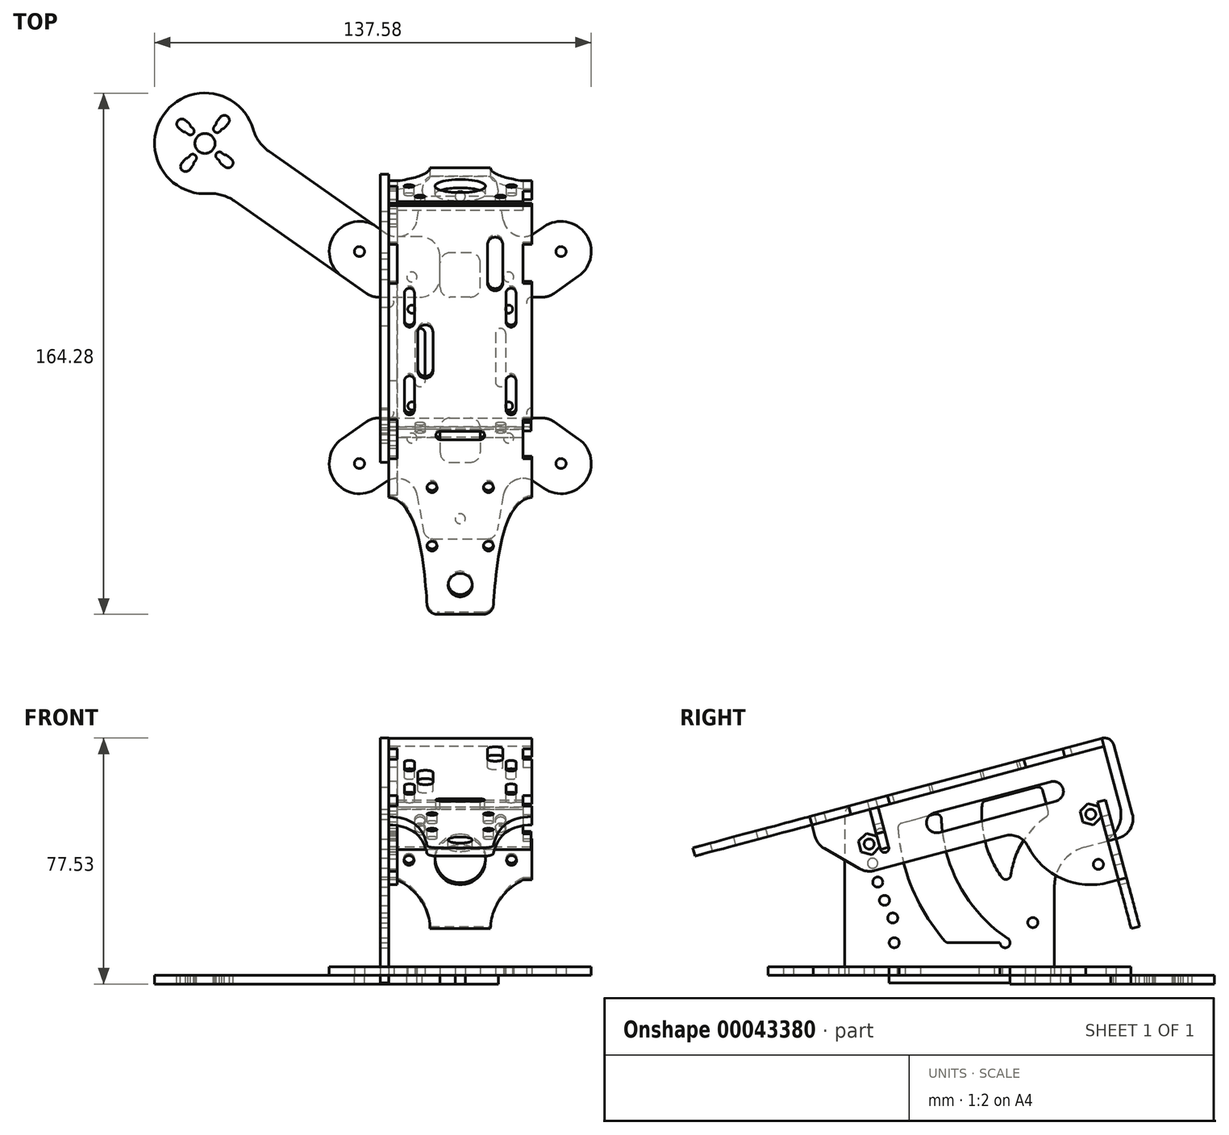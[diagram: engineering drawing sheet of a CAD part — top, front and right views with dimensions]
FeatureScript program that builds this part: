
annotation { "Feature Type Name" : "Feature", "Feature Type Description" : "" }
export const myFeature = defineFeature(function(context is Context, id is Id, definition is map)
    precondition{}
    {
        {
            var Q0;
            Q0=qCreatedBy(makeId("Top.planeOp"),FACE);
            var sketch = newSketch(context, id + "F0", { "sketchPlane" : qUnion([Q0])});
            skCircle(sketch, "E0", {"center": v(0, 0) * mm, "radius": 105 * mm, "construction": true});
            skLineSegment(sketch, "E1", {"start": v(0, 0) * mm, "end": v(-80.43, 67.5) * mm, "construction": true});
            skLineSegment(sketch, "E2", {"start": v(0, 0) * mm, "end": v(80.43, 67.5) * mm, "construction": true});
            skLineSegment(sketch, "E3", {"start": v(-80.43, 67.5) * mm, "end": v(80.43, 67.5) * mm, "construction": true});
            skLineSegment(sketch, "E4", {"start": v(0, 0) * mm, "end": v(80.43, -67.5) * mm, "construction": true});
            skLineSegment(sketch, "E5", {"start": v(80.43, -67.5) * mm, "end": v(-80.43, -67.5) * mm, "construction": true});
            skLineSegment(sketch, "E6", {"start": v(-80.43, -67.5) * mm, "end": v(0, 0) * mm, "construction": true});
            skSolve(sketch);
        }
        {
            var Q0;
            Q0=qCreatedBy(makeId("Top.planeOp"),FACE);
            var sketch = newSketch(context, id + "F1", { "sketchPlane" : qUnion([Q0])});
            skCircle(sketch, "E7", {"center": v(-80.43, 67.5) * mm, "radius": 15.88 * mm});
            skArc(sketch, "E8", {"start": v(-74.18, 60.17) * mm, "mid": v(-71.94, 60.37) * mm, "end": v(-72.14, 62.6) * mm});
            skArc(sketch, "E9", {"start": v(-75.88, 62.11) * mm, "mid": v(-75.7, 61.57) * mm, "end": v(-75.33, 61.13) * mm});
            skLineSegment(sketch, "E10", {"start": v(-80.43, 67.5) * mm, "end": v(-68.27, 57.29) * mm, "construction": true});
            skArc(sketch, "E11", {"start": v(-75.07, 64.55) * mm, "mid": v(-76.75, 64.4) * mm, "end": v(-76.6, 62.72) * mm});
            skLineSegment(sketch, "E12", {"start": v(-75.07, 64.55) * mm, "end": v(-74.35, 63.94) * mm});
            skLineSegment(sketch, "E13", {"start": v(-76.6, 62.72) * mm, "end": v(-75.88, 62.11) * mm});
            skLineSegment(sketch, "E14", {"start": v(-73.29, 63.57) * mm, "end": v(-72.14, 62.6) * mm});
            skLineSegment(sketch, "E15", {"start": v(-75.33, 61.13) * mm, "end": v(-74.18, 60.17) * mm});
            skArc(sketch, "E16.trimOffspring", {"start": v(-73.29, 63.57) * mm, "mid": v(-73.78, 63.85) * mm, "end": v(-74.35, 63.94) * mm});
            skArc(sketch, "E17.1.0", {"start": v(-77.5, 72.85) * mm, "mid": v(-77.34, 71.18) * mm, "end": v(-75.67, 71.32) * mm});
            skArc(sketch, "E17.1.1", {"start": v(-73.11, 73.75) * mm, "mid": v(-73.3, 75.99) * mm, "end": v(-75.54, 75.8) * mm});
            skArc(sketch, "E17.1.2", {"start": v(-76.5, 74.64) * mm, "mid": v(-76.8, 74.15) * mm, "end": v(-76.88, 73.58) * mm});
            skLineSegment(sketch, "E17.1.3", {"start": v(-74.08, 72.6) * mm, "end": v(-73.11, 73.75) * mm});
            skLineSegment(sketch, "E17.1.4", {"start": v(-76.5, 74.64) * mm, "end": v(-75.54, 75.8) * mm});
            skLineSegment(sketch, "E17.1.5", {"start": v(-75.67, 71.32) * mm, "end": v(-75.06, 72.05) * mm});
            skLineSegment(sketch, "E17.1.6", {"start": v(-77.5, 72.85) * mm, "end": v(-76.88, 73.58) * mm});
            skArc(sketch, "E17.1.7", {"start": v(-75.06, 72.05) * mm, "mid": v(-74.52, 72.24) * mm, "end": v(-74.08, 72.6) * mm});
            skArc(sketch, "E17.2.0", {"start": v(-85.8, 70.44) * mm, "mid": v(-84.12, 70.58) * mm, "end": v(-84.27, 72.26) * mm});
            skArc(sketch, "E17.2.1", {"start": v(-86.7, 74.82) * mm, "mid": v(-88.93, 74.62) * mm, "end": v(-88.73, 72.38) * mm});
            skArc(sketch, "E17.2.2", {"start": v(-87.58, 71.42) * mm, "mid": v(-87.09, 71.14) * mm, "end": v(-86.52, 71.05) * mm});
            skLineSegment(sketch, "E17.2.3", {"start": v(-85.54, 73.85) * mm, "end": v(-86.7, 74.82) * mm});
            skLineSegment(sketch, "E17.2.4", {"start": v(-87.58, 71.42) * mm, "end": v(-88.73, 72.38) * mm});
            skLineSegment(sketch, "E17.2.5", {"start": v(-84.27, 72.26) * mm, "end": v(-85, 72.87) * mm});
            skLineSegment(sketch, "E17.2.6", {"start": v(-85.8, 70.44) * mm, "end": v(-86.52, 71.05) * mm});
            skArc(sketch, "E17.2.7", {"start": v(-85, 72.87) * mm, "mid": v(-85.18, 73.41) * mm, "end": v(-85.54, 73.85) * mm});
            skArc(sketch, "E17.3.0", {"start": v(-83.38, 62.13) * mm, "mid": v(-83.53, 63.8) * mm, "end": v(-85.2, 63.66) * mm});
            skArc(sketch, "E17.3.1", {"start": v(-87.76, 61.24) * mm, "mid": v(-87.56, 59) * mm, "end": v(-85.33, 59.2) * mm});
            skArc(sketch, "E17.3.2", {"start": v(-84.36, 60.34) * mm, "mid": v(-84.08, 60.84) * mm, "end": v(-83.99, 61.4) * mm});
            skLineSegment(sketch, "E17.3.3", {"start": v(-86.8, 62.38) * mm, "end": v(-87.76, 61.24) * mm});
            skLineSegment(sketch, "E17.3.4", {"start": v(-84.36, 60.34) * mm, "end": v(-85.33, 59.2) * mm});
            skLineSegment(sketch, "E17.3.5", {"start": v(-85.2, 63.66) * mm, "end": v(-85.81, 62.93) * mm});
            skLineSegment(sketch, "E17.3.6", {"start": v(-83.38, 62.13) * mm, "end": v(-83.99, 61.4) * mm});
            skArc(sketch, "E17.3.7", {"start": v(-85.81, 62.93) * mm, "mid": v(-86.35, 62.75) * mm, "end": v(-86.8, 62.38) * mm});
            skCircle(sketch, "E18", {"center": v(-80.43, 67.5) * mm, "radius": 3.18 * mm});
            skCircle(sketch, "E19", {"center": v(-80.43, -67.5) * mm, "radius": 15.88 * mm});
            skLineSegment(sketch, "E20", {"start": v(-80.43, -67.5) * mm, "end": v(-70.23, -79.65) * mm, "construction": true});
            skCircle(sketch, "E21", {"center": v(-80.43, -67.5) * mm, "radius": 3.18 * mm});
            skArc(sketch, "E22.3.1", {"start": v(-88.73, -72.38) * mm, "mid": v(-88.93, -74.62) * mm, "end": v(-86.7, -74.82) * mm});
            skArc(sketch, "E23", {"start": v(-75.54, -75.8) * mm, "mid": v(-73.3, -75.99) * mm, "end": v(-73.11, -73.75) * mm});
            skArc(sketch, "E22.3.0", {"start": v(-84.27, -72.26) * mm, "mid": v(-84.12, -70.58) * mm, "end": v(-85.8, -70.44) * mm});
            skLineSegment(sketch, "E22.3.4", {"start": v(-85.54, -73.85) * mm, "end": v(-86.7, -74.82) * mm});
            skLineSegment(sketch, "E22.2.3", {"start": v(-84.36, -60.34) * mm, "end": v(-85.33, -59.2) * mm});
            skArc(sketch, "E22.2.1", {"start": v(-85.33, -59.2) * mm, "mid": v(-87.56, -59) * mm, "end": v(-87.76, -61.24) * mm});
            skArc(sketch, "E22.3.7", {"start": v(-86.52, -71.05) * mm, "mid": v(-87.09, -71.14) * mm, "end": v(-87.58, -71.42) * mm});
            skLineSegment(sketch, "E22.1.4", {"start": v(-75.33, -61.13) * mm, "end": v(-74.18, -60.17) * mm});
            skLineSegment(sketch, "E22.3.5", {"start": v(-85.8, -70.44) * mm, "end": v(-86.52, -71.05) * mm});
            skLineSegment(sketch, "E22.3.3", {"start": v(-87.58, -71.42) * mm, "end": v(-88.73, -72.38) * mm});
            skArc(sketch, "E24", {"start": v(-75.67, -71.32) * mm, "mid": v(-77.34, -71.18) * mm, "end": v(-77.5, -72.85) * mm});
            skLineSegment(sketch, "E22.3.6", {"start": v(-84.27, -72.26) * mm, "end": v(-85, -72.87) * mm});
            skArc(sketch, "E22.1.1", {"start": v(-72.14, -62.6) * mm, "mid": v(-71.94, -60.37) * mm, "end": v(-74.18, -60.17) * mm});
            skArc(sketch, "E22.3.2", {"start": v(-85.54, -73.85) * mm, "mid": v(-85.18, -73.41) * mm, "end": v(-85, -72.87) * mm});
            skLineSegment(sketch, "E22.2.6", {"start": v(-85.2, -63.66) * mm, "end": v(-85.81, -62.93) * mm});
            skArc(sketch, "E22.1.7", {"start": v(-74.35, -63.94) * mm, "mid": v(-73.78, -63.85) * mm, "end": v(-73.29, -63.57) * mm});
            skArc(sketch, "E22.2.7", {"start": v(-83.99, -61.4) * mm, "mid": v(-84.08, -60.84) * mm, "end": v(-84.36, -60.34) * mm});
            skLineSegment(sketch, "E22.1.3", {"start": v(-73.29, -63.57) * mm, "end": v(-72.14, -62.6) * mm});
            skLineSegment(sketch, "E22.2.5", {"start": v(-83.38, -62.13) * mm, "end": v(-83.99, -61.4) * mm});
            skLineSegment(sketch, "E22.1.5", {"start": v(-75.07, -64.55) * mm, "end": v(-74.35, -63.94) * mm});
            skLineSegment(sketch, "E22.2.4", {"start": v(-86.8, -62.38) * mm, "end": v(-87.76, -61.24) * mm});
            skArc(sketch, "E25", {"start": v(-76.88, -73.58) * mm, "mid": v(-76.8, -74.15) * mm, "end": v(-76.5, -74.64) * mm});
            skArc(sketch, "E22.2.2", {"start": v(-86.8, -62.38) * mm, "mid": v(-86.35, -62.75) * mm, "end": v(-85.81, -62.93) * mm});
            skArc(sketch, "E22.2.0", {"start": v(-85.2, -63.66) * mm, "mid": v(-83.53, -63.8) * mm, "end": v(-83.38, -62.13) * mm});
            skLineSegment(sketch, "E26", {"start": v(-77.5, -72.85) * mm, "end": v(-76.88, -73.58) * mm});
            skLineSegment(sketch, "E27", {"start": v(-74.08, -72.6) * mm, "end": v(-73.11, -73.75) * mm});
            skLineSegment(sketch, "E28", {"start": v(-76.5, -74.64) * mm, "end": v(-75.54, -75.8) * mm});
            skArc(sketch, "E29.trimOffspring", {"start": v(-74.08, -72.6) * mm, "mid": v(-74.52, -72.24) * mm, "end": v(-75.06, -72.05) * mm});
            skArc(sketch, "E22.1.0", {"start": v(-76.6, -62.72) * mm, "mid": v(-76.75, -64.4) * mm, "end": v(-75.07, -64.55) * mm});
            skArc(sketch, "E22.1.2", {"start": v(-75.33, -61.13) * mm, "mid": v(-75.7, -61.57) * mm, "end": v(-75.88, -62.11) * mm});
            skLineSegment(sketch, "E30", {"start": v(-75.67, -71.32) * mm, "end": v(-75.06, -72.05) * mm});
            skLineSegment(sketch, "E22.1.6", {"start": v(-76.6, -62.72) * mm, "end": v(-75.88, -62.11) * mm});
            skSolve(sketch);
        }
        {
            var Q0;
            Q0=qCreatedBy(makeId("Top.planeOp"),FACE);
            var sketch = newSketch(context, id + "F2", { "sketchPlane" : qUnion([Q0])});
            skCircle(sketch, "E31", {"center": v(-80.43, 67.5) * mm, "radius": 63.5 * mm, "construction": true});
            skLineSegment(sketch, "E32.bottom", {"start": v(-18, 18) * mm, "end": v(18, 18) * mm, "construction": true});
            skLineSegment(sketch, "E32.top", {"start": v(-18, -18) * mm, "end": v(18, -18) * mm, "construction": true});
            skLineSegment(sketch, "E32.left", {"start": v(-18, 18) * mm, "end": v(-18, -18) * mm, "construction": true});
            skLineSegment(sketch, "E32.right", {"start": v(18, 18) * mm, "end": v(18, -18) * mm, "construction": true});
            skPoint(sketch, "E33", {"position": v(0, 18) * mm});
            skPoint(sketch, "E34", {"position": v(18, 0) * mm});
            skCircle(sketch, "E35", {"center": v(-80.43, -67.5) * mm, "radius": 63.5 * mm, "construction": true});
            skCircle(sketch, "E36", {"center": v(80.43, -67.5) * mm, "radius": 63.5 * mm, "construction": true});
            skCircle(sketch, "E37", {"center": v(80.43, 67.5) * mm, "radius": 63.5 * mm, "construction": true});
            skSolve(sketch);
        }
        {
            var Q0;
            Q0=qCreatedBy(makeId("Top.planeOp"),FACE);
            var sketch = newSketch(context, id + "F3", { "sketchPlane" : qUnion([Q0])});
            skArc(sketch, "E38", {"start": v(-65.18, 71.88) * mm, "mid": v(-93.44, 76.6) * mm, "end": v(-79.34, 51.66) * mm});
            skLineSegment(sketch, "E39", {"start": v(-80.43, 67.5) * mm, "end": v(5.58, 7.27) * mm, "construction": true});
            skLineSegment(sketch, "E40.0", {"start": v(-71.19, 49.39) * mm, "end": v(-29.5, 20.2) * mm});
            skLineSegment(sketch, "E41.0", {"start": v(-60.26, 65) * mm, "end": v(-23.5, 39.25) * mm});
            skPoint(sketch, "E42.visualSharp", {"position": v(-64.57, 68.01) * mm});
            skArc(sketch, "E42.filletArc", {"start": v(-65.18, 71.88) * mm, "mid": v(-63.31, 68.02) * mm, "end": v(-60.26, 65) * mm});
            skPoint(sketch, "E43.visualSharp", {"position": v(-75.5, 52.4) * mm});
            skArc(sketch, "E43.filletArc", {"start": v(-71.19, 49.39) * mm, "mid": v(-75.07, 51.22) * mm, "end": v(-79.34, 51.66) * mm});
            skLineSegment(sketch, "E44", {"start": v(-12.7, 38.1) * mm, "end": v(-19.85, 38.1) * mm});
            skArc(sketch, "E45.filletArc", {"start": v(-23.5, 39.25) * mm, "mid": v(-21.76, 38.4) * mm, "end": v(-19.85, 38.1) * mm});
            skLineSegment(sketch, "E46", {"start": v(0, 0) * mm, "end": v(0, 111.42) * mm, "construction": true});
            skLineSegment(sketch, "E47", {"start": v(-22.5, -33.02) * mm, "end": v(-22.5, 33.02) * mm, "construction": true});
            skLineSegment(sketch, "E48", {"start": v(-25.86, 19.05) * mm, "end": v(-12.7, 19.05) * mm});
            skLineSegment(sketch, "E49", {"start": v(-6.35, 25.4) * mm, "end": v(-6.35, 31.75) * mm});
            skPoint(sketch, "E50.orphan", {"position": v(0, 19.05) * mm});
            skPoint(sketch, "E51.visualSharp", {"position": v(-6.35, 38.1) * mm});
            skArc(sketch, "E51.filletArc", {"start": v(-6.35, 31.75) * mm, "mid": v(-8.2, 36.24) * mm, "end": v(-12.7, 38.1) * mm});
            skPoint(sketch, "E52.visualSharp", {"position": v(-6.35, 19.05) * mm});
            skArc(sketch, "E52.filletArc", {"start": v(-12.7, 19.05) * mm, "mid": v(-8.2, 20.9) * mm, "end": v(-6.35, 25.4) * mm});
            skArc(sketch, "E53.filletArc", {"start": v(-29.5, 20.2) * mm, "mid": v(-27.76, 19.34) * mm, "end": v(-25.86, 19.05) * mm});
            skSolve(sketch);
        }
        {
            var Q0;
            Q0=qCreatedBy(makeId("Right.planeOp"),FACE);
            var sketch = newSketch(context, id + "F4", { "sketchPlane" : qUnion([Q0])});
            skLineSegment(sketch, "E54", {"start": v(-18.08, 54.87) * mm, "end": v(54.37, 74.29) * mm, "construction": true});
            skLineSegment(sketch, "E55", {"start": v(54.37, 74.29) * mm, "end": v(58.77, 57.87) * mm, "construction": true});
            skLineSegment(sketch, "E56", {"start": v(58.77, 57.87) * mm, "end": v(-13.68, 38.45) * mm, "construction": true});
            skLineSegment(sketch, "E57", {"start": v(-13.68, 38.45) * mm, "end": v(-18.08, 54.87) * mm, "construction": true});
            skLineSegment(sketch, "E58", {"start": v(33.02, 0) * mm, "end": v(33.02, 29.72) * mm});
            skCircle(sketch, "E59", {"center": v(50.8, 50.8) * mm, "radius": 1.59 * mm});
            skLineSegment(sketch, "E60", {"start": v(58.58, 46.3) * mm, "end": v(42.43, 41.98) * mm});
            skArc(sketch, "E61.filletArc", {"start": v(42.43, 41.98) * mm, "mid": v(35.64, 37.45) * mm, "end": v(33.02, 29.72) * mm});
            skLineSegment(sketch, "E62", {"start": v(63.07, 54.09) * mm, "end": v(58.14, 72.49) * mm});
            skArc(sketch, "E63.filletArc", {"start": v(58.58, 46.3) * mm, "mid": v(62.43, 49.27) * mm, "end": v(63.07, 54.09) * mm});
            skLineSegment(sketch, "E64", {"start": v(50.36, 76.98) * mm, "end": v(-28.31, 55.9) * mm});
            skLineSegment(sketch, "E65", {"start": v(0, 0) * mm, "end": v(135.9, 0) * mm, "construction": true});
            skPoint(sketch, "E66.visualSharp", {"position": v(56.5, 78.62) * mm});
            skArc(sketch, "E66.filletArc", {"start": v(58.14, 72.49) * mm, "mid": v(55.18, 76.34) * mm, "end": v(50.36, 76.98) * mm});
            skLineSegment(sketch, "E67", {"start": v(-33.02, 0) * mm, "end": v(-33.02, 49.76) * mm});
            skPoint(sketch, "E68.visualSharp", {"position": v(-33.02, 54.64) * mm});
            skArc(sketch, "E68.filletArc", {"start": v(-28.31, 55.9) * mm, "mid": v(-31.7, 53.63) * mm, "end": v(-33.02, 49.76) * mm});
            skCircle(sketch, "E69", {"center": v(50.8, 50.8) * mm, "radius": 77.48 * mm, "construction": true});
            skLineSegment(sketch, "E70", {"start": v(50.8, 50.8) * mm, "end": v(-26.67, 49.76) * mm, "construction": true});
            skLineSegment(sketch, "E71", {"start": v(50.8, 50.8) * mm, "end": v(-21.64, 23.33) * mm, "construction": true});
            skCircle(sketch, "E72.cCircle", {"center": v(50.8, 50.8) * mm, "radius": 3 * mm, "construction": true});
            skLineSegment(sketch, "E72.0", {"start": v(49.9, 54.15) * mm, "end": v(53.25, 53.25) * mm, "construction": true});
            skLineSegment(sketch, "E72.1", {"start": v(53.25, 53.25) * mm, "end": v(54.15, 49.9) * mm, "construction": true});
            skLineSegment(sketch, "E72.2", {"start": v(54.15, 49.9) * mm, "end": v(51.7, 47.45) * mm, "construction": true});
            skLineSegment(sketch, "E72.3", {"start": v(51.7, 47.45) * mm, "end": v(48.35, 48.35) * mm, "construction": true});
            skLineSegment(sketch, "E72.4", {"start": v(48.35, 48.35) * mm, "end": v(47.45, 51.7) * mm, "construction": true});
            skLineSegment(sketch, "E72.5", {"start": v(47.45, 51.7) * mm, "end": v(49.9, 54.15) * mm, "construction": true});
            skPoint(sketch, "E72.0.midPoint", {"position": v(51.58, 53.7) * mm});
            skCircle(sketch, "E73", {"center": v(-26.67, 49.76) * mm, "radius": 1.59 * mm});
            skLineSegment(sketch, "E74", {"start": v(50.8, 50.8) * mm, "end": v(-25.31, 36.33) * mm, "construction": true});
            skLineSegment(sketch, "E75", {"start": v(50.8, 50.8) * mm, "end": v(-23.76, 29.75) * mm, "construction": true});
            skCircle(sketch, "E76", {"center": v(-25.31, 36.33) * mm, "radius": 1.59 * mm});
            skCircle(sketch, "E77", {"center": v(-21.64, 23.33) * mm, "radius": 1.59 * mm});
            skLineSegment(sketch, "E78", {"start": v(50.8, 50.8) * mm, "end": v(-26.28, 43.02) * mm, "construction": true});
            skCircle(sketch, "E79", {"center": v(-26.28, 43.02) * mm, "radius": 1.59 * mm});
            skCircle(sketch, "E80", {"center": v(-23.76, 29.75) * mm, "radius": 1.59 * mm});
            skCircle(sketch, "E81.cCircle", {"center": v(-26.67, 49.76) * mm, "radius": 3 * mm, "construction": true});
            skLineSegment(sketch, "E81.0", {"start": v(-25.77, 53.11) * mm, "end": v(-23.32, 50.66) * mm, "construction": true});
            skLineSegment(sketch, "E81.1", {"start": v(-23.32, 50.66) * mm, "end": v(-24.22, 47.31) * mm, "construction": true});
            skLineSegment(sketch, "E81.2", {"start": v(-24.22, 47.31) * mm, "end": v(-27.57, 46.42) * mm, "construction": true});
            skLineSegment(sketch, "E81.3", {"start": v(-27.57, 46.42) * mm, "end": v(-30.02, 48.87) * mm, "construction": true});
            skLineSegment(sketch, "E81.4", {"start": v(-30.02, 48.87) * mm, "end": v(-29.12, 52.21) * mm, "construction": true});
            skLineSegment(sketch, "E81.5", {"start": v(-29.12, 52.21) * mm, "end": v(-25.77, 53.11) * mm, "construction": true});
            skPoint(sketch, "E81.0.midPoint", {"position": v(-24.55, 51.89) * mm});
            skLineSegment(sketch, "E82.0", {"start": v(51.06, 74.38) * mm, "end": v(-39.05, 50.23) * mm, "construction": true});
            skLineSegment(sketch, "E83", {"start": v(42.03, 71.96) * mm, "end": v(56.53, 17.82) * mm, "construction": true});
            skSolve(sketch);
        }
        {
            var Q0;
            Q0 = qSketchRegion(id + "F3", true);
            extrude(context, id + "F5", {"entities" : qUnion([Q0]), "oppositeDirection" : true, "depth" : 2.7 * mm});
        }
        {
            var Q0;
            Q0=makeQuery(id+"F5.opExtrude","CAP_FACE",FACE,{"disambiguationData":[OSD([sQuery(id+"F3.wireOp",EDGE,"E38"),sQuery(id+"F3.wireOp",EDGE,"E40.0"),sQuery(id+"F3.wireOp",EDGE,"E41.0"),sQuery(id+"F3.wireOp",EDGE,"E42.filletArc"),sQuery(id+"F3.wireOp",EDGE,"E43.filletArc"),sQuery(id+"F3.wireOp",EDGE,"E44"),sQuery(id+"F3.wireOp",EDGE,"E45.filletArc"),sQuery(id+"F3.wireOp",EDGE,"3483ba9e-9ece-47d6-9597-e3f51a3c630d"),sQuery(id+"F3.wireOp",EDGE,"183f9baa-443e-4921-8196-529d93f579a4"),sQuery(id+"F3.wireOp",EDGE,"E48"),sQuery(id+"F3.wireOp",EDGE,"dc9fa72e-4bdb-43c7-b6c3-07b077150070"),sQuery(id+"F3.wireOp",EDGE,"fd774d7d-7de3-4750-95d2-ba5d1b0ac5d5.filletArc"),sQuery(id+"F3.wireOp",EDGE,"888af924-2e86-4a76-b76f-690ec0a1ca8d.filletArc"),sQuery(id+"F3.wireOp",EDGE,"E49")])],"isStart":true});
            var sketch = newSketch(context, id + "F6", { "sketchPlane" : qUnion([Q0])});
            skLineSegment(sketch, "E84", {"start": v(-80.43, 67.5) * mm, "end": v(-31.75, 33.4) * mm, "construction": true});
            skCircle(sketch, "E85", {"center": v(-31.75, 33.4) * mm, "radius": 1.59 * mm});
            skArc(sketch, "E86.0", {"start": v(-77.5, 72.85) * mm, "mid": v(-77.34, 71.18) * mm, "end": v(-75.67, 71.32) * mm});
            skLineSegment(sketch, "E86.1", {"start": v(-77.5, 72.85) * mm, "end": v(-76.88, 73.58) * mm});
            skArc(sketch, "E86.2", {"start": v(-76.5, 74.64) * mm, "mid": v(-76.8, 74.15) * mm, "end": v(-76.88, 73.58) * mm});
            skLineSegment(sketch, "E86.3", {"start": v(-76.5, 74.64) * mm, "end": v(-75.54, 75.8) * mm});
            skArc(sketch, "E86.4", {"start": v(-73.11, 73.75) * mm, "mid": v(-73.3, 75.99) * mm, "end": v(-75.54, 75.8) * mm});
            skLineSegment(sketch, "E86.5", {"start": v(-74.08, 72.6) * mm, "end": v(-73.11, 73.75) * mm});
            skArc(sketch, "E86.6", {"start": v(-75.06, 72.05) * mm, "mid": v(-74.52, 72.24) * mm, "end": v(-74.08, 72.6) * mm});
            skLineSegment(sketch, "E86.7", {"start": v(-75.67, 71.32) * mm, "end": v(-75.06, 72.05) * mm});
            skArc(sketch, "E86.8", {"start": v(-75.07, 64.55) * mm, "mid": v(-76.75, 64.4) * mm, "end": v(-76.6, 62.72) * mm});
            skLineSegment(sketch, "E86.9", {"start": v(-75.07, 64.55) * mm, "end": v(-74.35, 63.94) * mm});
            skArc(sketch, "E86.10", {"start": v(-73.29, 63.57) * mm, "mid": v(-73.78, 63.85) * mm, "end": v(-74.35, 63.94) * mm});
            skLineSegment(sketch, "E86.11", {"start": v(-73.29, 63.57) * mm, "end": v(-72.14, 62.6) * mm});
            skArc(sketch, "E86.12", {"start": v(-74.18, 60.17) * mm, "mid": v(-71.94, 60.37) * mm, "end": v(-72.14, 62.6) * mm});
            skLineSegment(sketch, "E86.13", {"start": v(-75.33, 61.13) * mm, "end": v(-74.18, 60.17) * mm});
            skArc(sketch, "E86.14", {"start": v(-75.88, 62.11) * mm, "mid": v(-75.7, 61.57) * mm, "end": v(-75.33, 61.13) * mm});
            skLineSegment(sketch, "E86.15", {"start": v(-76.6, 62.72) * mm, "end": v(-75.88, 62.11) * mm});
            skCircle(sketch, "E86.16", {"center": v(-80.43, 67.5) * mm, "radius": 3.18 * mm});
            skArc(sketch, "E86.17", {"start": v(-85.8, 70.44) * mm, "mid": v(-84.12, 70.58) * mm, "end": v(-84.27, 72.26) * mm});
            skLineSegment(sketch, "E86.18", {"start": v(-85.8, 70.44) * mm, "end": v(-86.52, 71.05) * mm});
            skArc(sketch, "E86.19", {"start": v(-87.58, 71.42) * mm, "mid": v(-87.09, 71.14) * mm, "end": v(-86.52, 71.05) * mm});
            skLineSegment(sketch, "E86.20", {"start": v(-87.58, 71.42) * mm, "end": v(-88.73, 72.38) * mm});
            skArc(sketch, "E86.21", {"start": v(-86.7, 74.82) * mm, "mid": v(-88.93, 74.62) * mm, "end": v(-88.73, 72.38) * mm});
            skLineSegment(sketch, "E86.22", {"start": v(-85.54, 73.85) * mm, "end": v(-86.7, 74.82) * mm});
            skArc(sketch, "E86.23", {"start": v(-85, 72.87) * mm, "mid": v(-85.18, 73.41) * mm, "end": v(-85.54, 73.85) * mm});
            skLineSegment(sketch, "E86.24", {"start": v(-84.27, 72.26) * mm, "end": v(-85, 72.87) * mm});
            skArc(sketch, "E86.25", {"start": v(-83.38, 62.13) * mm, "mid": v(-83.53, 63.8) * mm, "end": v(-85.2, 63.66) * mm});
            skLineSegment(sketch, "E86.26", {"start": v(-85.2, 63.66) * mm, "end": v(-85.81, 62.93) * mm});
            skLineSegment(sketch, "E86.27", {"start": v(-83.38, 62.13) * mm, "end": v(-83.99, 61.4) * mm});
            skArc(sketch, "E86.28", {"start": v(-84.36, 60.34) * mm, "mid": v(-84.08, 60.84) * mm, "end": v(-83.99, 61.4) * mm});
            skLineSegment(sketch, "E86.29", {"start": v(-84.36, 60.34) * mm, "end": v(-85.33, 59.2) * mm});
            skArc(sketch, "E86.30", {"start": v(-87.76, 61.24) * mm, "mid": v(-87.56, 59) * mm, "end": v(-85.33, 59.2) * mm});
            skLineSegment(sketch, "E86.31", {"start": v(-86.8, 62.38) * mm, "end": v(-87.76, 61.24) * mm});
            skArc(sketch, "E86.32", {"start": v(-85.81, 62.93) * mm, "mid": v(-86.35, 62.75) * mm, "end": v(-86.8, 62.38) * mm});
            skCircle(sketch, "E87", {"center": v(-15.24, 25.4) * mm, "radius": 1.59 * mm});
            skSolve(sketch);
        }
        {
            var Q0;
            Q0 = qSketchRegion(id + "F6", true);
            var Q1;
            Q1=makeQuery(id+"F5.opExtrude","CAP_FACE",FACE,{"disambiguationData":[OSD([sQuery(id+"F3.wireOp",EDGE,"E38"),sQuery(id+"F3.wireOp",EDGE,"E40.0"),sQuery(id+"F3.wireOp",EDGE,"E41.0"),sQuery(id+"F3.wireOp",EDGE,"E42.filletArc"),sQuery(id+"F3.wireOp",EDGE,"E43.filletArc"),sQuery(id+"F3.wireOp",EDGE,"E44"),sQuery(id+"F3.wireOp",EDGE,"E45.filletArc"),sQuery(id+"F3.wireOp",EDGE,"3483ba9e-9ece-47d6-9597-e3f51a3c630d"),sQuery(id+"F3.wireOp",EDGE,"183f9baa-443e-4921-8196-529d93f579a4"),sQuery(id+"F3.wireOp",EDGE,"E48"),sQuery(id+"F3.wireOp",EDGE,"dc9fa72e-4bdb-43c7-b6c3-07b077150070"),sQuery(id+"F3.wireOp",EDGE,"fd774d7d-7de3-4750-95d2-ba5d1b0ac5d5.filletArc"),sQuery(id+"F3.wireOp",EDGE,"888af924-2e86-4a76-b76f-690ec0a1ca8d.filletArc"),sQuery(id+"F3.wireOp",EDGE,"E49")])],"isStart":false});
            extrude(context, id + "F7", {"entities" : qUnion([Q0]), "operationType" : NewBodyOperationType.REMOVE, "endBound" : BoundingType.UP_TO_SURFACE, "oppositeDirection" : true, "endBoundEntityFace" : qUnion([Q1]), "depth" : 25.4 * mm});
        }
        {
            var Q0;
            Q0=qCreatedBy(makeId("Top.planeOp"),FACE);
            var sketch = newSketch(context, id + "F8", { "sketchPlane" : qUnion([Q0])});
            skLineSegment(sketch, "E88.0", {"start": v(-37.21, 25.6) * mm, "end": v(-29.5, 20.2) * mm});
            skArc(sketch, "E88.1", {"start": v(-29.5, 20.2) * mm, "mid": v(-27.76, 19.34) * mm, "end": v(-25.86, 19.05) * mm});
            skLineSegment(sketch, "E88.2", {"start": v(-25.86, 19.05) * mm, "end": v(-22.5, 19.05) * mm});
            skLineSegment(sketch, "E88.3", {"start": v(-26.29, 41.2) * mm, "end": v(-23.5, 39.25) * mm});
            skArc(sketch, "E89", {"start": v(-26.29, 41.2) * mm, "mid": v(-39.55, 38.87) * mm, "end": v(-37.21, 25.6) * mm});
            skArc(sketch, "E90", {"start": v(-23.5, 39.25) * mm, "mid": v(-17.42, 38.58) * mm, "end": v(-13.6, 43.35) * mm});
            skLineSegment(sketch, "E91", {"start": v(-22.5, 0) * mm, "end": v(-22.5, 15.88) * mm});
            skArc(sketch, "E92", {"start": v(-22.5, 15.88) * mm, "mid": v(-20.92, 17.46) * mm, "end": v(-22.5, 19.05) * mm});
            skPoint(sketch, "E93.orphan", {"position": v(-12.7, 19.05) * mm});
            skLineSegment(sketch, "E94", {"start": v(-8.5, 57.15) * mm, "end": v(0, 57.15) * mm});
            skLineSegment(sketch, "E95", {"start": v(-13.6, 43.35) * mm, "end": v(-11.62, 54.53) * mm});
            skPoint(sketch, "E96.visualSharp", {"position": v(-11.16, 57.15) * mm});
            skArc(sketch, "E96.filletArc", {"start": v(-8.5, 57.15) * mm, "mid": v(-10.54, 56.4) * mm, "end": v(-11.62, 54.53) * mm});
            skLineSegment(sketch, "E97.MirrorCS", {"start": v(26.29, 41.2) * mm, "end": v(23.5, 39.25) * mm});
            skLineSegment(sketch, "E98.MirrorCS", {"start": v(25.86, 19.05) * mm, "end": v(22.5, 19.05) * mm});
            skArc(sketch, "E99.MirrorCS", {"start": v(29.5, 20.2) * mm, "mid": v(27.76, 19.34) * mm, "end": v(25.86, 19.05) * mm});
            skArc(sketch, "E100.MirrorCS", {"start": v(22.5, 15.88) * mm, "mid": v(20.92, 17.46) * mm, "end": v(22.5, 19.05) * mm});
            skArc(sketch, "E101.MirrorCS", {"start": v(8.5, 57.15) * mm, "mid": v(10.54, 56.4) * mm, "end": v(11.62, 54.53) * mm});
            skLineSegment(sketch, "E102.MirrorCS", {"start": v(8.5, 57.15) * mm, "end": v(0, 57.15) * mm});
            skPoint(sketch, "E103.MirrorP", {"position": v(11.16, 57.15) * mm});
            skLineSegment(sketch, "E104.MirrorCS", {"start": v(13.6, 43.35) * mm, "end": v(11.62, 54.53) * mm});
            skArc(sketch, "E105.MirrorCS", {"start": v(23.5, 39.25) * mm, "mid": v(17.42, 38.58) * mm, "end": v(13.6, 43.35) * mm});
            skArc(sketch, "E106.MirrorCS", {"start": v(26.29, 41.2) * mm, "mid": v(39.55, 38.87) * mm, "end": v(37.21, 25.6) * mm});
            skLineSegment(sketch, "E107.MirrorCS", {"start": v(37.21, 25.6) * mm, "end": v(29.5, 20.2) * mm});
            skPoint(sketch, "E108.MirrorP", {"position": v(12.7, 19.05) * mm});
            skLineSegment(sketch, "E109.MirrorCS", {"start": v(22.5, 0) * mm, "end": v(22.5, 15.88) * mm});
            skArc(sketch, "E110.MirrorCS", {"start": v(-8.5, -57.15) * mm, "mid": v(-10.54, -56.4) * mm, "end": v(-11.62, -54.53) * mm});
            skArc(sketch, "E111.MirrorCS", {"start": v(8.5, -57.15) * mm, "mid": v(10.54, -56.4) * mm, "end": v(11.62, -54.53) * mm});
            skLineSegment(sketch, "E112.MirrorCS", {"start": v(-26.29, -41.2) * mm, "end": v(-23.5, -39.25) * mm});
            skLineSegment(sketch, "E113.MirrorCS", {"start": v(26.29, -41.2) * mm, "end": v(23.5, -39.25) * mm});
            skLineSegment(sketch, "E114.MirrorCS", {"start": v(-37.21, -25.6) * mm, "end": v(-29.5, -20.2) * mm});
            skArc(sketch, "E115.MirrorCS", {"start": v(-29.5, -20.2) * mm, "mid": v(-27.76, -19.34) * mm, "end": v(-25.86, -19.05) * mm});
            skArc(sketch, "E116.MirrorCS", {"start": v(29.5, -20.2) * mm, "mid": v(27.76, -19.34) * mm, "end": v(25.86, -19.05) * mm});
            skLineSegment(sketch, "E117.MirrorCS", {"start": v(25.86, -19.05) * mm, "end": v(22.5, -19.05) * mm});
            skLineSegment(sketch, "E118.MirrorCS", {"start": v(-25.86, -19.05) * mm, "end": v(-22.5, -19.05) * mm});
            skArc(sketch, "E119.MirrorCS", {"start": v(22.5, -15.88) * mm, "mid": v(20.92, -17.46) * mm, "end": v(22.5, -19.05) * mm});
            skLineSegment(sketch, "E120.MirrorCS", {"start": v(-8.5, -57.15) * mm, "end": v(0, -57.15) * mm});
            skPoint(sketch, "E121.MirrorP", {"position": v(-11.16, -57.15) * mm});
            skLineSegment(sketch, "E122.MirrorCS", {"start": v(8.5, -57.15) * mm, "end": v(0, -57.15) * mm});
            skPoint(sketch, "E123.MirrorP", {"position": v(11.16, -57.15) * mm});
            skLineSegment(sketch, "E124.MirrorCS", {"start": v(13.6, -43.35) * mm, "end": v(11.62, -54.53) * mm});
            skLineSegment(sketch, "E125.MirrorCS", {"start": v(-13.6, -43.35) * mm, "end": v(-11.62, -54.53) * mm});
            skArc(sketch, "E126.MirrorCS", {"start": v(23.5, -39.25) * mm, "mid": v(17.42, -38.58) * mm, "end": v(13.6, -43.35) * mm});
            skArc(sketch, "E127.MirrorCS", {"start": v(-23.5, -39.25) * mm, "mid": v(-17.42, -38.58) * mm, "end": v(-13.6, -43.35) * mm});
            skArc(sketch, "E128.MirrorCS", {"start": v(26.29, -41.2) * mm, "mid": v(39.55, -38.87) * mm, "end": v(37.21, -25.6) * mm});
            skArc(sketch, "E129.MirrorCS", {"start": v(-26.29, -41.2) * mm, "mid": v(-39.55, -38.87) * mm, "end": v(-37.21, -25.6) * mm});
            skLineSegment(sketch, "E130.MirrorCS", {"start": v(37.21, -25.6) * mm, "end": v(29.5, -20.2) * mm});
            skPoint(sketch, "E131.MirrorP", {"position": v(-12.7, -19.05) * mm});
            skArc(sketch, "E132.MirrorCS", {"start": v(-22.5, -15.88) * mm, "mid": v(-20.92, -17.46) * mm, "end": v(-22.5, -19.05) * mm});
            skPoint(sketch, "E133.MirrorP", {"position": v(12.7, -19.05) * mm});
            skLineSegment(sketch, "E134.MirrorCS", {"start": v(22.5, 0) * mm, "end": v(22.5, -15.88) * mm});
            skLineSegment(sketch, "E135.MirrorCS", {"start": v(-22.5, 0) * mm, "end": v(-22.5, -15.88) * mm});
            skSolve(sketch);
        }
        {
            var Q0;
            Q0 = qSketchRegion(id + "F8", true);
            extrude(context, id + "F9", {"entities" : qUnion([Q0]), "depth" : 2.7 * mm});
        }
        {
            var Q0;
            Q0=qCreatedBy(makeId("Top.planeOp"),FACE);
            var sketch = newSketch(context, id + "F10", { "sketchPlane" : qUnion([Q0])});
            skLineSegment(sketch, "E136", {"start": v(-15.25, 15.25) * mm, "end": v(-15.25, 0) * mm, "construction": true});
            skCircle(sketch, "E137", {"center": v(-15.25, 15.25) * mm, "radius": 1.27 * mm});
            skLineSegment(sketch, "E138", {"start": v(0, 19.05) * mm, "end": v(-3.17, 19.05) * mm});
            skLineSegment(sketch, "E139", {"start": v(-6.35, 22.23) * mm, "end": v(-6.35, 29.85) * mm});
            skLineSegment(sketch, "E140", {"start": v(-3.17, 33.02) * mm, "end": v(0, 33.02) * mm});
            skPoint(sketch, "E141.visualSharp", {"position": v(-6.35, 19.05) * mm});
            skArc(sketch, "E141.filletArc", {"start": v(-6.35, 22.23) * mm, "mid": v(-5.42, 19.98) * mm, "end": v(-3.17, 19.05) * mm});
            skPoint(sketch, "E142.visualSharp", {"position": v(-6.35, 33.02) * mm});
            skArc(sketch, "E142.filletArc", {"start": v(-3.18, 33.02) * mm, "mid": v(-5.42, 32.1) * mm, "end": v(-6.35, 29.85) * mm});
            skCircle(sketch, "E143.0", {"center": v(-15.24, 25.4) * mm, "radius": 1.59 * mm});
            skCircle(sketch, "E143.1", {"center": v(-31.75, 33.4) * mm, "radius": 1.59 * mm});
            skLineSegment(sketch, "E144.MirrorCS", {"start": v(0, 19.05) * mm, "end": v(3.17, 19.05) * mm});
            skArc(sketch, "E145.MirrorCS", {"start": v(3.18, 33.02) * mm, "mid": v(5.42, 32.1) * mm, "end": v(6.35, 29.85) * mm});
            skArc(sketch, "E146.MirrorCS", {"start": v(6.35, 22.23) * mm, "mid": v(5.42, 19.98) * mm, "end": v(3.17, 19.05) * mm});
            skLineSegment(sketch, "E147.MirrorCS", {"start": v(6.35, 22.23) * mm, "end": v(6.35, 29.85) * mm});
            skLineSegment(sketch, "E148.MirrorCS", {"start": v(3.17, 33.02) * mm, "end": v(0, 33.02) * mm});
            skCircle(sketch, "E149.MirrorC", {"center": v(31.75, 33.4) * mm, "radius": 1.59 * mm});
            skCircle(sketch, "E150.MirrorC", {"center": v(15.24, 25.4) * mm, "radius": 1.59 * mm});
            skCircle(sketch, "E151.MirrorC", {"center": v(15.25, 15.25) * mm, "radius": 1.27 * mm});
            skPoint(sketch, "E152.MirrorP", {"position": v(6.35, 33.02) * mm});
            skPoint(sketch, "E153.MirrorP", {"position": v(6.35, 19.05) * mm});
            skLineSegment(sketch, "E154.MirrorCS", {"start": v(3.17, -33.02) * mm, "end": v(0, -33.02) * mm});
            skLineSegment(sketch, "E155.MirrorCS", {"start": v(-3.17, -33.02) * mm, "end": v(0, -33.02) * mm});
            skLineSegment(sketch, "E156.MirrorCS", {"start": v(0, -19.05) * mm, "end": v(3.17, -19.05) * mm});
            skLineSegment(sketch, "E157.MirrorCS", {"start": v(0, -19.05) * mm, "end": v(-3.17, -19.05) * mm});
            skArc(sketch, "E158.MirrorCS", {"start": v(3.18, -33.02) * mm, "mid": v(5.42, -32.1) * mm, "end": v(6.35, -29.85) * mm});
            skArc(sketch, "E159.MirrorCS", {"start": v(6.35, -22.23) * mm, "mid": v(5.42, -19.98) * mm, "end": v(3.17, -19.05) * mm});
            skArc(sketch, "E160.MirrorCS", {"start": v(-6.35, -22.23) * mm, "mid": v(-5.42, -19.98) * mm, "end": v(-3.17, -19.05) * mm});
            skArc(sketch, "E161.MirrorCS", {"start": v(-3.18, -33.02) * mm, "mid": v(-5.42, -32.1) * mm, "end": v(-6.35, -29.85) * mm});
            skPoint(sketch, "E162.MirrorP", {"position": v(6.35, -33.02) * mm});
            skPoint(sketch, "E163.MirrorP", {"position": v(-6.35, -33.02) * mm});
            skCircle(sketch, "E164.MirrorC", {"center": v(-31.75, -33.4) * mm, "radius": 1.59 * mm});
            skCircle(sketch, "E165.MirrorC", {"center": v(31.75, -33.4) * mm, "radius": 1.59 * mm});
            skLineSegment(sketch, "E166.MirrorCS", {"start": v(6.35, -22.23) * mm, "end": v(6.35, -29.85) * mm});
            skLineSegment(sketch, "E167.MirrorCS", {"start": v(-6.35, -22.23) * mm, "end": v(-6.35, -29.85) * mm});
            skCircle(sketch, "E168.MirrorC", {"center": v(15.24, -25.4) * mm, "radius": 1.59 * mm});
            skCircle(sketch, "E169.MirrorC", {"center": v(-15.24, -25.4) * mm, "radius": 1.59 * mm});
            skPoint(sketch, "E170.MirrorP", {"position": v(6.35, -19.05) * mm});
            skPoint(sketch, "E171.MirrorP", {"position": v(-6.35, -19.05) * mm});
            skCircle(sketch, "E172.MirrorC", {"center": v(15.25, -15.25) * mm, "radius": 1.27 * mm});
            skCircle(sketch, "E173.MirrorC", {"center": v(-15.25, -15.25) * mm, "radius": 1.27 * mm});
            skLineSegment(sketch, "E174", {"start": v(-12.7, 7.62) * mm, "end": v(-12.7, -7.62) * mm, "construction": true});
            skPoint(sketch, "E175", {"position": v(-12.7, 0) * mm});
            skArc(sketch, "E176", {"start": v(-11.11, 7.62) * mm, "mid": v(-12.7, 9.2) * mm, "end": v(-14.29, 7.62) * mm});
            skArc(sketch, "E177", {"start": v(-14.29, -7.62) * mm, "mid": v(-12.7, -9.2) * mm, "end": v(-11.11, -7.62) * mm});
            skLineSegment(sketch, "E178.0", {"start": v(-14.29, 7.62) * mm, "end": v(-14.29, -7.62) * mm});
            skLineSegment(sketch, "E179.0", {"start": v(-11.11, 7.62) * mm, "end": v(-11.11, -7.62) * mm});
            skLineSegment(sketch, "E180.MirrorCS", {"start": v(11.11, 7.62) * mm, "end": v(11.11, -7.62) * mm});
            skLineSegment(sketch, "E181.MirrorCS", {"start": v(12.7, 7.62) * mm, "end": v(12.7, -7.62) * mm, "construction": true});
            skArc(sketch, "E182.MirrorCS", {"start": v(11.11, 7.62) * mm, "mid": v(12.7, 9.2) * mm, "end": v(14.29, 7.62) * mm});
            skArc(sketch, "E183.MirrorCS", {"start": v(14.29, -7.62) * mm, "mid": v(12.7, -9.2) * mm, "end": v(11.11, -7.62) * mm});
            skPoint(sketch, "E184.MirrorP", {"position": v(12.7, 0) * mm});
            skLineSegment(sketch, "E185.MirrorCS", {"start": v(14.29, 7.62) * mm, "end": v(14.29, -7.62) * mm});
            skCircle(sketch, "E186", {"center": v(0, 50.8) * mm, "radius": 1.59 * mm});
            skCircle(sketch, "E187", {"center": v(0, -50.8) * mm, "radius": 1.59 * mm});
            skSolve(sketch);
        }
        {
            var Q0;
            Q0 = qSketchRegion(id + "F10", true);
            var Q1;
            Q1=makeQuery(id+"F9.opExtrude","CAP_FACE",FACE,{"disambiguationData":[OSD([sQuery(id+"F8.wireOp",EDGE,"E88.0"),sQuery(id+"F8.wireOp",EDGE,"E88.1"),sQuery(id+"F8.wireOp",EDGE,"E88.2"),sQuery(id+"F8.wireOp",EDGE,"E88.3"),sQuery(id+"F8.wireOp",EDGE,"E89"),sQuery(id+"F8.wireOp",EDGE,"E90"),sQuery(id+"F8.wireOp",EDGE,"E91"),sQuery(id+"F8.wireOp",EDGE,"E92"),sQuery(id+"F8.wireOp",EDGE,"E94"),sQuery(id+"F8.wireOp",EDGE,"E95"),sQuery(id+"F8.wireOp",EDGE,"E96.filletArc"),sQuery(id+"F8.wireOp",EDGE,"E97.MirrorCS"),sQuery(id+"F8.wireOp",EDGE,"E98.MirrorCS"),sQuery(id+"F8.wireOp",EDGE,"E99.MirrorCS"),sQuery(id+"F8.wireOp",EDGE,"E100.MirrorCS"),sQuery(id+"F8.wireOp",EDGE,"E101.MirrorCS"),sQuery(id+"F8.wireOp",EDGE,"E102.MirrorCS"),sQuery(id+"F8.wireOp",EDGE,"E104.MirrorCS"),sQuery(id+"F8.wireOp",EDGE,"E105.MirrorCS"),sQuery(id+"F8.wireOp",EDGE,"E106.MirrorCS"),sQuery(id+"F8.wireOp",EDGE,"E107.MirrorCS"),sQuery(id+"F8.wireOp",EDGE,"E109.MirrorCS"),sQuery(id+"F8.wireOp",EDGE,"E110.MirrorCS"),sQuery(id+"F8.wireOp",EDGE,"E111.MirrorCS"),sQuery(id+"F8.wireOp",EDGE,"E112.MirrorCS"),sQuery(id+"F8.wireOp",EDGE,"E113.MirrorCS"),sQuery(id+"F8.wireOp",EDGE,"E114.MirrorCS"),sQuery(id+"F8.wireOp",EDGE,"E115.MirrorCS"),sQuery(id+"F8.wireOp",EDGE,"E116.MirrorCS"),sQuery(id+"F8.wireOp",EDGE,"E117.MirrorCS"),sQuery(id+"F8.wireOp",EDGE,"E118.MirrorCS"),sQuery(id+"F8.wireOp",EDGE,"E119.MirrorCS"),sQuery(id+"F8.wireOp",EDGE,"E120.MirrorCS"),sQuery(id+"F8.wireOp",EDGE,"E122.MirrorCS"),sQuery(id+"F8.wireOp",EDGE,"E124.MirrorCS"),sQuery(id+"F8.wireOp",EDGE,"E125.MirrorCS"),sQuery(id+"F8.wireOp",EDGE,"E126.MirrorCS"),sQuery(id+"F8.wireOp",EDGE,"E127.MirrorCS"),sQuery(id+"F8.wireOp",EDGE,"E128.MirrorCS"),sQuery(id+"F8.wireOp",EDGE,"E129.MirrorCS"),sQuery(id+"F8.wireOp",EDGE,"E130.MirrorCS"),sQuery(id+"F8.wireOp",EDGE,"E132.MirrorCS"),sQuery(id+"F8.wireOp",EDGE,"E134.MirrorCS"),sQuery(id+"F8.wireOp",EDGE,"E135.MirrorCS")])],"isStart":false});
            extrude(context, id + "F11", {"entities" : qUnion([Q0]), "operationType" : NewBodyOperationType.REMOVE, "endBound" : BoundingType.UP_TO_SURFACE, "endBoundEntityFace" : qUnion([Q1]), "depth" : 25.4 * mm});
        }
        {
            var Q0;
            Q0=makeQuery(id+"F9.opExtrude","SWEPT_FACE",FACE,{"disambiguationData":[OSD([sQuery(id+"F8.wireOp",EDGE,"E91"),sQuery(id+"F8.wireOp",EDGE,"E135.MirrorCS")])]});
            var sketch = newSketch(context, id + "F12", { "sketchPlane" : qUnion([Q0])});
            skLineSegment(sketch, "E188", {"start": v(-33.02, 2.7) * mm, "end": v(-33.02, 28.13) * mm});
            skLineSegment(sketch, "E189", {"start": v(-42.43, 40.4) * mm, "end": v(-53.05, 43.24) * mm});
            skLineSegment(sketch, "E190", {"start": v(-57.54, 51.02) * mm, "end": v(-51.79, 72.49) * mm});
            skLineSegment(sketch, "E191", {"start": v(-47.9, 74.73) * mm, "end": v(30.67, 53.68) * mm});
            skLineSegment(sketch, "E192", {"start": v(33.02, 50.61) * mm, "end": v(33.02, 2.7) * mm});
            skLineSegment(sketch, "E193", {"start": v(33.02, 2.7) * mm, "end": v(19.05, 2.7) * mm});
            skLineSegment(sketch, "E194", {"start": v(19.05, 2.7) * mm, "end": v(19.05, -2.39) * mm});
            skLineSegment(sketch, "E195", {"start": v(19.05, -2.39) * mm, "end": v(-19.05, -2.39) * mm});
            skLineSegment(sketch, "E196", {"start": v(-19.05, -2.39) * mm, "end": v(-19.05, 2.7) * mm});
            skLineSegment(sketch, "E197", {"start": v(-19.05, 2.7) * mm, "end": v(-33.02, 2.7) * mm});
            skPoint(sketch, "E198", {"position": v(-44.45, 50.8) * mm});
            skPoint(sketch, "E199.visualSharp", {"position": v(-59.18, 44.89) * mm});
            skArc(sketch, "E199.filletArc", {"start": v(-57.54, 51.02) * mm, "mid": v(-56.9, 46.2) * mm, "end": v(-53.05, 43.24) * mm});
            skPoint(sketch, "E200.visualSharp", {"position": v(-50.97, 75.55) * mm});
            skArc(sketch, "E200.filletArc", {"start": v(-47.9, 74.73) * mm, "mid": v(-50.3, 74.42) * mm, "end": v(-51.79, 72.49) * mm});
            skPoint(sketch, "E201.visualSharp", {"position": v(33.02, 53.05) * mm});
            skArc(sketch, "E201.filletArc", {"start": v(33.02, 50.61) * mm, "mid": v(32.36, 52.55) * mm, "end": v(30.67, 53.68) * mm});
            skPoint(sketch, "E202.visualSharp", {"position": v(-33.02, 37.88) * mm});
            skArc(sketch, "E202.filletArc", {"start": v(-33.02, 28.13) * mm, "mid": v(-35.64, 35.86) * mm, "end": v(-42.43, 40.4) * mm});
            skLineSegment(sketch, "E203", {"start": v(-44.45, 50.8) * mm, "end": v(23.02, 32.72) * mm, "construction": true});
            skLineSegment(sketch, "E204.0", {"start": v(-42.12, 59.5) * mm, "end": v(25.35, 41.41) * mm, "construction": true});
            skSolve(sketch);
        }
        {
            var Q0;
            Q0 = qSketchRegion(id + "F12", true);
            extrude(context, id + "F13", {"entities" : qUnion([Q0]), "depth" : 2.7 * mm});
        }
        {
            var Q0;
            Q0=makeQuery(id+"F13.opExtrude","CAP_FACE",FACE,{"disambiguationData":[OSD([sQuery(id+"F12.wireOp",EDGE,"E188"),sQuery(id+"F12.wireOp",EDGE,"E189"),sQuery(id+"F12.wireOp",EDGE,"E190"),sQuery(id+"F12.wireOp",EDGE,"E191"),sQuery(id+"F12.wireOp",EDGE,"E192"),sQuery(id+"F12.wireOp",EDGE,"E193"),sQuery(id+"F12.wireOp",EDGE,"E194"),sQuery(id+"F12.wireOp",EDGE,"E195"),sQuery(id+"F12.wireOp",EDGE,"E196"),sQuery(id+"F12.wireOp",EDGE,"E197"),sQuery(id+"F12.wireOp",EDGE,"E199.filletArc"),sQuery(id+"F12.wireOp",EDGE,"E200.filletArc"),sQuery(id+"F12.wireOp",EDGE,"E201.filletArc"),sQuery(id+"F12.wireOp",EDGE,"E202.filletArc")])],"isStart":true});
            var sketch = newSketch(context, id + "F14", { "sketchPlane" : qUnion([Q0])});
            skCircle(sketch, "E205", {"center": v(44.45, 50.8) * mm, "radius": 1.59 * mm});
            skCircle(sketch, "E206", {"center": v(-25.35, 41.41) * mm, "radius": 1.59 * mm});
            skCircle(sketch, "E207", {"center": v(44.45, 50.8) * mm, "radius": 70.43 * mm, "construction": true});
            skLineSegment(sketch, "E208", {"start": v(44.45, 50.8) * mm, "end": v(-25.35, 41.41) * mm, "construction": true});
            skLineSegment(sketch, "E209", {"start": v(44.45, 50.8) * mm, "end": v(-24.27, 35.37) * mm, "construction": true});
            skLineSegment(sketch, "E210", {"start": v(44.45, 50.8) * mm, "end": v(-22.66, 29.44) * mm, "construction": true});
            skLineSegment(sketch, "E211", {"start": v(44.45, 50.8) * mm, "end": v(-20.54, 23.67) * mm, "construction": true});
            skLineSegment(sketch, "E212", {"start": v(44.45, 50.8) * mm, "end": v(-17.93, 18.1) * mm, "construction": true});
            skCircle(sketch, "E213", {"center": v(-24.27, 35.37) * mm, "radius": 1.59 * mm});
            skCircle(sketch, "E214", {"center": v(-22.66, 29.44) * mm, "radius": 1.59 * mm});
            skCircle(sketch, "E215", {"center": v(-20.54, 23.67) * mm, "radius": 1.59 * mm});
            skCircle(sketch, "E216", {"center": v(-17.93, 18.1) * mm, "radius": 1.59 * mm});
            skCircle(sketch, "E217", {"center": v(26.2, 16.66) * mm, "radius": 1.59 * mm});
            skLineSegment(sketch, "E218.0", {"start": v(-4.6, 50.8) * mm, "end": v(-15.12, 47.99) * mm});
            skArc(sketch, "E219.0", {"start": v(-16.29, 46.34) * mm, "mid": v(-11.78, 27.4) * mm, "end": v(-1.53, 10.86) * mm});
            skLineSegment(sketch, "E220.0", {"start": v(31.06, 51.7) * mm, "end": v(29.3, 58.25) * mm});
            skArc(sketch, "E221", {"start": v(15.88, 10.31) * mm, "mid": v(18.21, 8.91) * mm, "end": v(18.34, 11.63) * mm});
            skCircle(sketch, "E222", {"center": v(-17.46, 10.31) * mm, "radius": 1.59 * mm});
            skLineSegment(sketch, "E223", {"start": v(15.88, 10.31) * mm, "end": v(-0.33, 10.31) * mm});
            skArc(sketch, "E224", {"start": v(-2.6, 49.32) * mm, "mid": v(3.3, 27.94) * mm, "end": v(18.34, 11.63) * mm});
            skArc(sketch, "E225.filletArc", {"start": v(-2.6, 49.32) * mm, "mid": v(-3.24, 50.55) * mm, "end": v(-4.6, 50.8) * mm});
            skPoint(sketch, "E226.visualSharp", {"position": v(-16.37, 47.65) * mm});
            skArc(sketch, "E226.filletArc", {"start": v(-15.12, 47.99) * mm, "mid": v(-16, 47.37) * mm, "end": v(-16.29, 46.34) * mm});
            skPoint(sketch, "E227.visualSharp", {"position": v(-1.05, 10.31) * mm});
            skArc(sketch, "E227.filletArc", {"start": v(-1.53, 10.86) * mm, "mid": v(-0.99, 10.46) * mm, "end": v(-0.33, 10.31) * mm});
            skArc(sketch, "E228", {"start": v(30.44, 49.99) * mm, "mid": v(22.93, 41.98) * mm, "end": v(19.28, 31.63) * mm});
            skArc(sketch, "E229.0", {"start": v(10.2, 53.68) * mm, "mid": v(11.3, 41.75) * mm, "end": v(16.41, 30.92) * mm});
            skLineSegment(sketch, "E230", {"start": v(11.37, 55.08) * mm, "end": v(27.36, 59.37) * mm});
            skPoint(sketch, "E231.visualSharp", {"position": v(28.9, 59.78) * mm});
            skArc(sketch, "E231.filletArc", {"start": v(29.3, 58.25) * mm, "mid": v(28.57, 59.21) * mm, "end": v(27.36, 59.37) * mm});
            skPoint(sketch, "E232.visualSharp", {"position": v(31.36, 50.6) * mm});
            skArc(sketch, "E232.filletArc", {"start": v(30.44, 49.99) * mm, "mid": v(31.02, 50.75) * mm, "end": v(31.06, 51.7) * mm});
            skArc(sketch, "E233.filletArc", {"start": v(11.37, 55.08) * mm, "mid": v(10.57, 54.57) * mm, "end": v(10.2, 53.68) * mm});
            skPoint(sketch, "E234.visualSharp", {"position": v(19.05, 27.64) * mm});
            skArc(sketch, "E234.filletArc", {"start": v(16.41, 30.92) * mm, "mid": v(18.09, 30.3) * mm, "end": v(19.28, 31.63) * mm});
            skSolve(sketch);
        }
        {
            var Q0;
            Q0 = qSketchRegion(id + "F14", true);
            var Q1;
            Q1=makeQuery(id+"F13.opExtrude","CAP_FACE",FACE,{"disambiguationData":[OSD([sQuery(id+"F12.wireOp",EDGE,"E188"),sQuery(id+"F12.wireOp",EDGE,"E189"),sQuery(id+"F12.wireOp",EDGE,"E190"),sQuery(id+"F12.wireOp",EDGE,"E191"),sQuery(id+"F12.wireOp",EDGE,"E192"),sQuery(id+"F12.wireOp",EDGE,"E193"),sQuery(id+"F12.wireOp",EDGE,"E194"),sQuery(id+"F12.wireOp",EDGE,"E195"),sQuery(id+"F12.wireOp",EDGE,"E196"),sQuery(id+"F12.wireOp",EDGE,"E197"),sQuery(id+"F12.wireOp",EDGE,"E199.filletArc"),sQuery(id+"F12.wireOp",EDGE,"E200.filletArc"),sQuery(id+"F12.wireOp",EDGE,"E201.filletArc"),sQuery(id+"F12.wireOp",EDGE,"E202.filletArc")])],"isStart":false});
            extrude(context, id + "F15", {"entities" : qUnion([Q0]), "operationType" : NewBodyOperationType.REMOVE, "endBound" : BoundingType.UP_TO_SURFACE, "oppositeDirection" : true, "endBoundEntityFace" : qUnion([Q1]), "depth" : 25.4 * mm});
        }
        {
            var Q0;
            Q0=makeQuery(id+"F12.imprint","IMPRINT",FACE,{"disambiguationData":[TD([[makeQuery(id+"F12.imprint","IMPRINT",EDGE,{"derivedFrom":sQuery(id+"F12.wireOp",EDGE,"E188")}),-1.0]])]});
            var sketch = newSketch(context, id + "F16", { "sketchPlane" : qUnion([Q0])});
            skLineSegment(sketch, "E235", {"start": v(-48.6, 72.13) * mm, "end": v(-53.65, 53.27) * mm});
            skArc(sketch, "E236", {"start": v(-53.65, 53.27) * mm, "mid": v(-53.35, 47.41) * mm, "end": v(-49.69, 42.84) * mm});
            skCircle(sketch, "E237.cCircle", {"center": v(-44.45, 50.8) * mm, "radius": 3 * mm, "construction": true});
            skLineSegment(sketch, "E237.0", {"start": v(-47.8, 49.9) * mm, "end": v(-46.9, 53.25) * mm, "construction": true});
            skLineSegment(sketch, "E237.1", {"start": v(-46.9, 53.25) * mm, "end": v(-43.55, 54.15) * mm, "construction": true});
            skLineSegment(sketch, "E237.2", {"start": v(-43.55, 54.15) * mm, "end": v(-41.1, 51.7) * mm, "construction": true});
            skLineSegment(sketch, "E237.3", {"start": v(-41.1, 51.7) * mm, "end": v(-42, 48.35) * mm, "construction": true});
            skLineSegment(sketch, "E237.4", {"start": v(-42, 48.35) * mm, "end": v(-45.35, 47.45) * mm, "construction": true});
            skLineSegment(sketch, "E237.5", {"start": v(-45.35, 47.45) * mm, "end": v(-47.8, 49.9) * mm, "construction": true});
            skPoint(sketch, "E237.0.midPoint", {"position": v(-47.35, 51.58) * mm});
            skLineSegment(sketch, "E238", {"start": v(-49.69, 42.84) * mm, "end": v(-53.1, 30.1) * mm});
            skLineSegment(sketch, "E239", {"start": v(-48.6, 72.13) * mm, "end": v(-36.33, 68.85) * mm});
            skLineSegment(sketch, "E240", {"start": v(43.4, 47.48) * mm, "end": v(42.45, 43.89) * mm});
            skLineSegment(sketch, "E241", {"start": v(23.67, 33.05) * mm, "end": v(-17.31, 44.03) * mm});
            skLineSegment(sketch, "E242", {"start": v(-53.1, 30.1) * mm, "end": v(-50.2, 29.33) * mm});
            skArc(sketch, "E243", {"start": v(-50.2, 29.33) * mm, "mid": v(-35.38, 30.5) * mm, "end": v(-24.62, 40.76) * mm});
            skPoint(sketch, "E244.visualSharp", {"position": v(-22.86, 45.52) * mm});
            skArc(sketch, "E244.filletArc", {"start": v(-17.31, 44.03) * mm, "mid": v(-21.55, 43.7) * mm, "end": v(-24.62, 40.76) * mm});
            skLineSegment(sketch, "E245", {"start": v(-35.63, 71.45) * mm, "end": v(-23.36, 68.16) * mm});
            skLineSegment(sketch, "E246", {"start": v(-23.36, 68.16) * mm, "end": v(-24.06, 65.56) * mm});
            skLineSegment(sketch, "E247", {"start": v(31.14, 50.77) * mm, "end": v(31.84, 53.37) * mm});
            skLineSegment(sketch, "E248", {"start": v(31.84, 53.37) * mm, "end": v(19.57, 56.65) * mm});
            skLineSegment(sketch, "E249", {"start": v(19.57, 56.65) * mm, "end": v(18.87, 54.05) * mm});
            skLineSegment(sketch, "E250", {"start": v(-36.33, 68.85) * mm, "end": v(-35.63, 71.45) * mm});
            skLineSegment(sketch, "E251.trimOffspring", {"start": v(-24.06, 65.56) * mm, "end": v(18.87, 54.05) * mm});
            skLineSegment(sketch, "E252.trimOffspring", {"start": v(31.14, 50.77) * mm, "end": v(43.4, 47.48) * mm});
            skLineSegment(sketch, "E253", {"start": v(39.49, 40.03) * mm, "end": v(28.49, 33.68) * mm});
            skPoint(sketch, "E254.visualSharp", {"position": v(41.77, 41.35) * mm});
            skArc(sketch, "E254.filletArc", {"start": v(39.49, 40.03) * mm, "mid": v(41.35, 41.66) * mm, "end": v(42.45, 43.89) * mm});
            skPoint(sketch, "E255.visualSharp", {"position": v(26.21, 32.37) * mm});
            skArc(sketch, "E255.filletArc", {"start": v(23.67, 33.05) * mm, "mid": v(26.14, 32.88) * mm, "end": v(28.49, 33.68) * mm});
            skSolve(sketch);
        }
        {
            var Q0;
            Q0 = qSketchRegion(id + "F16", true);
            extrude(context, id + "F17", {"entities" : qUnion([Q0]), "oppositeDirection" : true, "depth" : 2.7 * mm});
        }
        {
            var Q0;
            Q0=makeQuery(id+"F17.opExtrude","CAP_FACE",FACE,{"disambiguationData":[OSD([sQuery(id+"F16.wireOp",EDGE,"E235"),sQuery(id+"F16.wireOp",EDGE,"E236"),sQuery(id+"F16.wireOp",EDGE,"E238"),sQuery(id+"F16.wireOp",EDGE,"E239"),sQuery(id+"F16.wireOp",EDGE,"E240"),sQuery(id+"F16.wireOp",EDGE,"E241"),sQuery(id+"F16.wireOp",EDGE,"e16bc254-febc-42ca-a439-24e0f454c1e5"),sQuery(id+"F16.wireOp",EDGE,"E242"),sQuery(id+"F16.wireOp",EDGE,"E243"),sQuery(id+"F16.wireOp",EDGE,"E244.filletArc"),sQuery(id+"F16.wireOp",EDGE,"E245"),sQuery(id+"F16.wireOp",EDGE,"E246"),sQuery(id+"F16.wireOp",EDGE,"E247"),sQuery(id+"F16.wireOp",EDGE,"E248"),sQuery(id+"F16.wireOp",EDGE,"E249"),sQuery(id+"F16.wireOp",EDGE,"E250"),sQuery(id+"F16.wireOp",EDGE,"E251.trimOffspring"),sQuery(id+"F16.wireOp",EDGE,"E252.trimOffspring")])],"isStart":true});
            var sketch = newSketch(context, id + "F18", { "sketchPlane" : qUnion([Q0])});
            skCircle(sketch, "E256.cCircle", {"center": v(-44.45, 50.8) * mm, "radius": 3 * mm, "construction": true});
            skLineSegment(sketch, "E256.0", {"start": v(-47.8, 49.9) * mm, "end": v(-46.9, 53.25) * mm});
            skLineSegment(sketch, "E256.1", {"start": v(-46.9, 53.25) * mm, "end": v(-43.55, 54.15) * mm});
            skLineSegment(sketch, "E256.2", {"start": v(-43.55, 54.15) * mm, "end": v(-41.1, 51.7) * mm});
            skLineSegment(sketch, "E256.3", {"start": v(-41.1, 51.7) * mm, "end": v(-42, 48.35) * mm});
            skLineSegment(sketch, "E256.4", {"start": v(-42, 48.35) * mm, "end": v(-45.35, 47.45) * mm});
            skLineSegment(sketch, "E256.5", {"start": v(-45.35, 47.45) * mm, "end": v(-47.8, 49.9) * mm});
            skPoint(sketch, "E256.0.midPoint", {"position": v(-47.35, 51.58) * mm});
            skCircle(sketch, "E257.cCircle", {"center": v(25.35, 41.41) * mm, "radius": 3 * mm, "construction": true});
            skLineSegment(sketch, "E257.0", {"start": v(22.9, 43.86) * mm, "end": v(26.25, 44.76) * mm});
            skLineSegment(sketch, "E257.1", {"start": v(26.25, 44.76) * mm, "end": v(28.7, 42.31) * mm});
            skLineSegment(sketch, "E257.2", {"start": v(28.7, 42.31) * mm, "end": v(27.8, 38.97) * mm});
            skLineSegment(sketch, "E257.3", {"start": v(27.8, 38.97) * mm, "end": v(24.45, 38.07) * mm});
            skLineSegment(sketch, "E257.4", {"start": v(24.45, 38.07) * mm, "end": v(22, 40.52) * mm});
            skPoint(sketch, "E257.0.midPoint", {"position": v(24.57, 44.31) * mm});
            skLineSegment(sketch, "E258", {"start": v(19.2, 40.43) * mm, "end": v(20.5, 45.34) * mm});
            skLineSegment(sketch, "E259", {"start": v(23.1, 44.64) * mm, "end": v(22.9, 43.86) * mm});
            skLineSegment(sketch, "E260", {"start": v(22, 40.52) * mm, "end": v(21.8, 39.74) * mm});
            skPoint(sketch, "E261", {"position": v(19.85, 42.89) * mm});
            skArc(sketch, "E262", {"start": v(23.1, 44.64) * mm, "mid": v(22.16, 46.3) * mm, "end": v(20.5, 45.34) * mm});
            skArc(sketch, "E263", {"start": v(19.2, 40.43) * mm, "mid": v(20.15, 38.79) * mm, "end": v(21.8, 39.74) * mm});
            skLineSegment(sketch, "E264", {"start": v(21.8, 45) * mm, "end": v(20.5, 40.09) * mm, "construction": true});
            skLineSegment(sketch, "E265", {"start": v(23.1, 44.64) * mm, "end": v(20.5, 45.34) * mm, "construction": true});
            skLineSegment(sketch, "E266", {"start": v(21.8, 39.74) * mm, "end": v(19.2, 40.43) * mm, "construction": true});
            skCircle(sketch, "E267", {"center": v(-46.86, 35) * mm, "radius": 1.59 * mm});
            skLineSegment(sketch, "E268.0", {"start": v(-31.84, 61.07) * mm, "end": v(4.96, 51.2) * mm});
            skLineSegment(sketch, "E269.0", {"start": v(3.32, 45.07) * mm, "end": v(-33.48, 54.93) * mm});
            skArc(sketch, "E270", {"start": v(-31.84, 61.07) * mm, "mid": v(-35.73, 58.82) * mm, "end": v(-33.48, 54.93) * mm});
            skArc(sketch, "E271", {"start": v(3.32, 45.07) * mm, "mid": v(7.2, 47.32) * mm, "end": v(4.96, 51.2) * mm});
            skSolve(sketch);
        }
        {
            var Q0;
            Q0 = qSketchRegion(id + "F18", true);
            var Q1;
            Q1=makeQuery(id+"F17.opExtrude","CAP_FACE",FACE,{"disambiguationData":[OSD([sQuery(id+"F16.wireOp",EDGE,"E235"),sQuery(id+"F16.wireOp",EDGE,"E236"),sQuery(id+"F16.wireOp",EDGE,"E238"),sQuery(id+"F16.wireOp",EDGE,"E239"),sQuery(id+"F16.wireOp",EDGE,"E240"),sQuery(id+"F16.wireOp",EDGE,"E241"),sQuery(id+"F16.wireOp",EDGE,"e16bc254-febc-42ca-a439-24e0f454c1e5"),sQuery(id+"F16.wireOp",EDGE,"E242"),sQuery(id+"F16.wireOp",EDGE,"E243"),sQuery(id+"F16.wireOp",EDGE,"E244.filletArc"),sQuery(id+"F16.wireOp",EDGE,"E245"),sQuery(id+"F16.wireOp",EDGE,"E246"),sQuery(id+"F16.wireOp",EDGE,"E247"),sQuery(id+"F16.wireOp",EDGE,"E248"),sQuery(id+"F16.wireOp",EDGE,"E249"),sQuery(id+"F16.wireOp",EDGE,"E250"),sQuery(id+"F16.wireOp",EDGE,"E251.trimOffspring"),sQuery(id+"F16.wireOp",EDGE,"E252.trimOffspring")])],"isStart":false});
            extrude(context, id + "F19", {"entities" : qUnion([Q0]), "operationType" : NewBodyOperationType.REMOVE, "endBound" : BoundingType.UP_TO_SURFACE, "oppositeDirection" : true, "endBoundEntityFace" : qUnion([Q1]), "depth" : 25.4 * mm});
        }
        {
            var Q0;
            Q0=makeQuery(id+"F17.opExtrude","SWEPT_FACE",FACE,{"disambiguationData":[OSD([sQuery(id+"F16.wireOp",EDGE,"E251.trimOffspring")])]});
            var sketch = newSketch(context, id + "F20", { "sketchPlane" : qUnion([Q0])});
            skLineSegment(sketch, "E272", {"start": v(-22.5, 65.6) * mm, "end": v(0, 65.6) * mm});
            skLineSegment(sketch, "E273", {"start": v(-22.5, 65.6) * mm, "end": v(-22.5, 52.9) * mm});
            skLineSegment(sketch, "E274", {"start": v(-22.5, 52.9) * mm, "end": v(-19.81, 52.9) * mm});
            skLineSegment(sketch, "E275", {"start": v(-19.81, 52.9) * mm, "end": v(-19.81, 40.2) * mm});
            skLineSegment(sketch, "E276", {"start": v(-19.81, 40.2) * mm, "end": v(-22.5, 40.2) * mm});
            skLineSegment(sketch, "E277", {"start": v(-22.5, 40.2) * mm, "end": v(-22.5, -4.24) * mm});
            skLineSegment(sketch, "E278", {"start": v(-22.5, -4.24) * mm, "end": v(-19.81, -4.24) * mm});
            skLineSegment(sketch, "E279", {"start": v(-19.81, -4.24) * mm, "end": v(-19.81, -16.94) * mm});
            skLineSegment(sketch, "E280", {"start": v(-19.81, -16.94) * mm, "end": v(-22.5, -16.94) * mm});
            skLineSegment(sketch, "E281", {"start": v(-22.5, -16.94) * mm, "end": v(-22.5, -29.64) * mm});
            skLineSegment(sketch, "E282", {"start": v(0, -67.74) * mm, "end": v(-7.28, -67.74) * mm});
            skFitSpline(sketch, "E283", {"points": [v(-22.5, -29.64) * mm, v(-10.16, -67.74) * mm], "startDerivative": vector(34.3, -3.81) * mm, "endDerivative": vector(2.67, -19.05) * mm});
            skArc(sketch, "E284.filletArc", {"start": v(-10.44, -64.8) * mm, "mid": v(-9.43, -66.9) * mm, "end": v(-7.28, -67.74) * mm});
            skArc(sketch, "E285.MirrorCS", {"start": v(10.44, -64.8) * mm, "mid": v(9.43, -66.9) * mm, "end": v(7.28, -67.74) * mm});
            skLineSegment(sketch, "E286.MirrorCS", {"start": v(22.5, 52.9) * mm, "end": v(19.81, 52.9) * mm});
            skLineSegment(sketch, "E287.MirrorCS", {"start": v(19.81, 40.2) * mm, "end": v(22.5, 40.2) * mm});
            skLineSegment(sketch, "E288.MirrorCS", {"start": v(22.5, -4.24) * mm, "end": v(19.81, -4.24) * mm});
            skLineSegment(sketch, "E289.MirrorCS", {"start": v(19.81, -16.94) * mm, "end": v(22.5, -16.94) * mm});
            skLineSegment(sketch, "E290.MirrorCS", {"start": v(0, -67.74) * mm, "end": v(7.28, -67.74) * mm});
            skLineSegment(sketch, "E291.MirrorCS", {"start": v(22.5, 65.6) * mm, "end": v(0, 65.6) * mm});
            skLineSegment(sketch, "E292.MirrorCS", {"start": v(22.5, 65.6) * mm, "end": v(22.5, 52.9) * mm});
            skLineSegment(sketch, "E293.MirrorCS", {"start": v(19.81, 52.9) * mm, "end": v(19.81, 40.2) * mm});
            skLineSegment(sketch, "E294.MirrorCS", {"start": v(22.5, 40.2) * mm, "end": v(22.5, -4.24) * mm});
            skLineSegment(sketch, "E295.MirrorCS", {"start": v(19.81, -4.24) * mm, "end": v(19.81, -16.94) * mm});
            skLineSegment(sketch, "E296.MirrorCS", {"start": v(22.5, -16.94) * mm, "end": v(22.5, -29.64) * mm});
            skFitSpline(sketch, "E297.MirrorCS", {"points": [v(22.5, -29.64) * mm, v(10.16, -67.74) * mm], "startDerivative": vector(-34.3, -3.81) * mm, "endDerivative": vector(-2.67, -19.05) * mm});
            skSolve(sketch);
        }
        {
            var Q0;
            Q0 = qSketchRegion(id + "F20", true);
            extrude(context, id + "F21", {"entities" : qUnion([Q0]), "depth" : 2.7 * mm});
        }
        {
            var Q0;
            Q0=makeQuery(id+"F21.opExtrude","CAP_FACE",FACE,{"disambiguationData":[OSD([sQuery(id+"F20.wireOp",EDGE,"E272"),sQuery(id+"F20.wireOp",EDGE,"E273"),sQuery(id+"F20.wireOp",EDGE,"E274"),sQuery(id+"F20.wireOp",EDGE,"E275"),sQuery(id+"F20.wireOp",EDGE,"E276"),sQuery(id+"F20.wireOp",EDGE,"E277"),sQuery(id+"F20.wireOp",EDGE,"E278"),sQuery(id+"F20.wireOp",EDGE,"E279"),sQuery(id+"F20.wireOp",EDGE,"E280"),sQuery(id+"F20.wireOp",EDGE,"E281"),sQuery(id+"F20.wireOp",EDGE,"E282"),sQuery(id+"F20.wireOp",EDGE,"E283"),sQuery(id+"F20.wireOp",EDGE,"E284.filletArc"),sQuery(id+"F20.wireOp",EDGE,"E285.MirrorCS"),sQuery(id+"F20.wireOp",EDGE,"E286.MirrorCS"),sQuery(id+"F20.wireOp",EDGE,"E287.MirrorCS"),sQuery(id+"F20.wireOp",EDGE,"E288.MirrorCS"),sQuery(id+"F20.wireOp",EDGE,"E289.MirrorCS"),sQuery(id+"F20.wireOp",EDGE,"E290.MirrorCS"),sQuery(id+"F20.wireOp",EDGE,"E291.MirrorCS"),sQuery(id+"F20.wireOp",EDGE,"E292.MirrorCS"),sQuery(id+"F20.wireOp",EDGE,"E293.MirrorCS"),sQuery(id+"F20.wireOp",EDGE,"E294.MirrorCS"),sQuery(id+"F20.wireOp",EDGE,"E295.MirrorCS"),sQuery(id+"F20.wireOp",EDGE,"E296.MirrorCS"),sQuery(id+"F20.wireOp",EDGE,"E297.MirrorCS")])],"isStart":false});
            var sketch = newSketch(context, id + "F22", { "sketchPlane" : qUnion([Q0])});
            skLineSegment(sketch, "E298", {"start": v(-16, 65.6) * mm, "end": v(-16, -56.86) * mm, "construction": true});
            skArc(sketch, "E299", {"start": v(-14.41, 37.03) * mm, "mid": v(-16, 38.62) * mm, "end": v(-17.59, 37.03) * mm});
            skArc(sketch, "E300", {"start": v(-17.59, 27.5) * mm, "mid": v(-16, 25.92) * mm, "end": v(-14.41, 27.5) * mm});
            skArc(sketch, "E301", {"start": v(-14.41, 8.46) * mm, "mid": v(-16, 10.05) * mm, "end": v(-17.59, 8.46) * mm});
            skArc(sketch, "E302", {"start": v(-17.59, -1.07) * mm, "mid": v(-16, -2.65) * mm, "end": v(-14.41, -1.07) * mm});
            skLineSegment(sketch, "E303", {"start": v(-17.59, 37.03) * mm, "end": v(-17.59, 27.5) * mm});
            skLineSegment(sketch, "E304", {"start": v(-14.41, 37.03) * mm, "end": v(-14.41, 27.5) * mm});
            skLineSegment(sketch, "E305", {"start": v(-17.59, 8.46) * mm, "end": v(-17.59, -1.07) * mm});
            skLineSegment(sketch, "E306", {"start": v(-14.41, 8.46) * mm, "end": v(-14.41, -1.07) * mm});
            skLineSegment(sketch, "E307", {"start": v(-11, 65.6) * mm, "end": v(-11, -5.35) * mm, "construction": true});
            skArc(sketch, "E308", {"start": v(-8.62, 24.33) * mm, "mid": v(-11, 26.71) * mm, "end": v(-13.38, 24.33) * mm});
            skArc(sketch, "E309", {"start": v(-13.38, 11.63) * mm, "mid": v(-11, 9.25) * mm, "end": v(-8.62, 11.63) * mm});
            skLineSegment(sketch, "E310", {"start": v(-13.38, 24.33) * mm, "end": v(-13.38, 11.63) * mm});
            skLineSegment(sketch, "E311", {"start": v(-8.62, 24.33) * mm, "end": v(-8.62, 11.63) * mm});
            skCircle(sketch, "E312", {"center": v(0, -58.22) * mm, "radius": 3.81 * mm});
            skArc(sketch, "E313.MirrorCS", {"start": v(14.41, 37.03) * mm, "mid": v(16, 38.62) * mm, "end": v(17.59, 37.03) * mm});
            skLineSegment(sketch, "E314.MirrorCS", {"start": v(14.41, 37.03) * mm, "end": v(14.41, 27.5) * mm});
            skLineSegment(sketch, "E315.MirrorCS", {"start": v(17.59, 37.03) * mm, "end": v(17.59, 27.5) * mm});
            skArc(sketch, "E316.MirrorCS", {"start": v(17.59, 27.5) * mm, "mid": v(16, 25.92) * mm, "end": v(14.41, 27.5) * mm});
            skArc(sketch, "E317.MirrorCS", {"start": v(14.41, 8.46) * mm, "mid": v(16, 10.05) * mm, "end": v(17.59, 8.46) * mm});
            skLineSegment(sketch, "E318.MirrorCS", {"start": v(14.41, 8.46) * mm, "end": v(14.41, -1.07) * mm});
            skLineSegment(sketch, "E319.MirrorCS", {"start": v(17.59, 8.46) * mm, "end": v(17.59, -1.07) * mm});
            skArc(sketch, "E320.MirrorCS", {"start": v(17.59, -1.07) * mm, "mid": v(16, -2.65) * mm, "end": v(14.41, -1.07) * mm});
            skLineSegment(sketch, "E321", {"start": v(11, 65.6) * mm, "end": v(11, -4.31) * mm, "construction": true});
            skPoint(sketch, "E322", {"position": v(11, 40.2) * mm});
            skArc(sketch, "E323", {"start": v(8.62, 40.2) * mm, "mid": v(11, 37.83) * mm, "end": v(13.38, 40.2) * mm});
            skLineSegment(sketch, "E324", {"start": v(8.62, 52.9) * mm, "end": v(8.62, 40.2) * mm});
            skArc(sketch, "E325", {"start": v(13.38, 52.9) * mm, "mid": v(11, 55.29) * mm, "end": v(8.62, 52.9) * mm});
            skLineSegment(sketch, "E326", {"start": v(13.38, 52.9) * mm, "end": v(13.38, 40.2) * mm});
            skLineSegment(sketch, "E327", {"start": v(-8.9, -26.47) * mm, "end": v(-8.9, -45.52) * mm, "construction": true});
            skCircle(sketch, "E328", {"center": v(-8.9, -45.52) * mm, "radius": 1.59 * mm});
            skCircle(sketch, "E329", {"center": v(-8.9, -26.47) * mm, "radius": 1.59 * mm});
            skCircle(sketch, "E330.MirrorC", {"center": v(8.9, -26.47) * mm, "radius": 1.59 * mm});
            skLineSegment(sketch, "E331.MirrorCS", {"start": v(8.9, -26.47) * mm, "end": v(8.89, -45.52) * mm, "construction": true});
            skCircle(sketch, "E332.MirrorC", {"center": v(8.89, -45.52) * mm, "radius": 1.59 * mm});
            skLineSegment(sketch, "E333", {"start": v(-6.35, -10.77) * mm, "end": v(6.35, -10.77) * mm});
            skPoint(sketch, "E334", {"position": v(0, -10.77) * mm});
            skLineSegment(sketch, "E335.0", {"start": v(-6.35, -8.07) * mm, "end": v(6.35, -8.07) * mm});
            skArc(sketch, "E336", {"start": v(-6.35, -8.07) * mm, "mid": v(-7.7, -9.42) * mm, "end": v(-6.35, -10.77) * mm});
            skArc(sketch, "E337", {"start": v(6.35, -10.77) * mm, "mid": v(7.7, -9.42) * mm, "end": v(6.35, -8.07) * mm});
            skSolve(sketch);
        }
        {
            var Q0;
            Q0 = qSketchRegion(id + "F22", true);
            var Q1;
            Q1=makeQuery(id+"F21.opExtrude","CAP_FACE",FACE,{"disambiguationData":[OSD([sQuery(id+"F20.wireOp",EDGE,"E272"),sQuery(id+"F20.wireOp",EDGE,"E273"),sQuery(id+"F20.wireOp",EDGE,"E274"),sQuery(id+"F20.wireOp",EDGE,"E275"),sQuery(id+"F20.wireOp",EDGE,"E276"),sQuery(id+"F20.wireOp",EDGE,"E277"),sQuery(id+"F20.wireOp",EDGE,"E278"),sQuery(id+"F20.wireOp",EDGE,"E279"),sQuery(id+"F20.wireOp",EDGE,"E280"),sQuery(id+"F20.wireOp",EDGE,"E281"),sQuery(id+"F20.wireOp",EDGE,"E282"),sQuery(id+"F20.wireOp",EDGE,"E283"),sQuery(id+"F20.wireOp",EDGE,"E284.filletArc"),sQuery(id+"F20.wireOp",EDGE,"E285.MirrorCS"),sQuery(id+"F20.wireOp",EDGE,"E286.MirrorCS"),sQuery(id+"F20.wireOp",EDGE,"E287.MirrorCS"),sQuery(id+"F20.wireOp",EDGE,"E288.MirrorCS"),sQuery(id+"F20.wireOp",EDGE,"E289.MirrorCS"),sQuery(id+"F20.wireOp",EDGE,"E290.MirrorCS"),sQuery(id+"F20.wireOp",EDGE,"E291.MirrorCS"),sQuery(id+"F20.wireOp",EDGE,"E292.MirrorCS"),sQuery(id+"F20.wireOp",EDGE,"E293.MirrorCS"),sQuery(id+"F20.wireOp",EDGE,"E294.MirrorCS"),sQuery(id+"F20.wireOp",EDGE,"E295.MirrorCS"),sQuery(id+"F20.wireOp",EDGE,"E296.MirrorCS"),sQuery(id+"F20.wireOp",EDGE,"E297.MirrorCS")])],"isStart":true});
            extrude(context, id + "F23", {"entities" : qUnion([Q0]), "operationType" : NewBodyOperationType.REMOVE, "endBound" : BoundingType.UP_TO_SURFACE, "oppositeDirection" : true, "endBoundEntityFace" : qUnion([Q1]), "depth" : 25.4 * mm});
        }
        {
            var Q0;
            Q0=makeQuery(id+"F17.opExtrude","SWEPT_FACE",FACE,{"disambiguationData":[OSD([sQuery(id+"F16.wireOp",EDGE,"E238")])]});
            var sketch = newSketch(context, id + "F24", { "sketchPlane" : qUnion([Q0])});
            skLineSegment(sketch, "E338", {"start": v(19.81, 40.74) * mm, "end": v(0, 40.74) * mm});
            skLineSegment(sketch, "E339", {"start": v(19.81, 40.74) * mm, "end": v(19.81, 28.04) * mm});
            skLineSegment(sketch, "E340", {"start": v(19.81, 28.04) * mm, "end": v(22.5, 28.04) * mm});
            skLineSegment(sketch, "E341", {"start": v(22.5, 28.04) * mm, "end": v(22.5, 15.34) * mm});
            skLineSegment(sketch, "E342", {"start": v(22.5, 15.34) * mm, "end": v(19.81, 15.34) * mm});
            skLineSegment(sketch, "E343", {"start": v(0, -0.54) * mm, "end": v(9.53, -0.54) * mm});
            skFitSpline(sketch, "E344", {"points": [v(19.81, 15.34) * mm, v(9.53, -0.54) * mm], "startDerivative": vector(-19.05, -9.52) * mm, "endDerivative": vector(0, -19.05) * mm});
            skLineSegment(sketch, "E345.MirrorCS", {"start": v(-22.5, 15.34) * mm, "end": v(-19.81, 15.34) * mm});
            skLineSegment(sketch, "E346.MirrorCS", {"start": v(-19.81, 28.04) * mm, "end": v(-22.5, 28.04) * mm});
            skLineSegment(sketch, "E347.MirrorCS", {"start": v(-19.81, 40.74) * mm, "end": v(0, 40.74) * mm});
            skLineSegment(sketch, "E348.MirrorCS", {"start": v(-19.81, 40.74) * mm, "end": v(-19.81, 28.04) * mm});
            skLineSegment(sketch, "E349.MirrorCS", {"start": v(-22.5, 28.04) * mm, "end": v(-22.5, 15.34) * mm});
            skFitSpline(sketch, "E350.MirrorCS", {"points": [v(-19.81, 15.34) * mm, v(-9.53, -0.54) * mm], "startDerivative": vector(19.05, -9.52) * mm, "endDerivative": vector(0, -19.05) * mm});
            skLineSegment(sketch, "E351.MirrorCS", {"start": v(0, -0.54) * mm, "end": v(-9.53, -0.54) * mm});
            skSolve(sketch);
        }
        {
            var Q0;
            Q0 = qSketchRegion(id + "F24", true);
            extrude(context, id + "F25", {"entities" : qUnion([Q0]), "depth" : 2.7 * mm});
        }
        {
            var Q0;
            Q0=makeQuery(id+"F25.opExtrude","CAP_FACE",FACE,{"disambiguationData":[OSD([sQuery(id+"F24.wireOp",EDGE,"E338"),sQuery(id+"F24.wireOp",EDGE,"E339"),sQuery(id+"F24.wireOp",EDGE,"E340"),sQuery(id+"F24.wireOp",EDGE,"E341"),sQuery(id+"F24.wireOp",EDGE,"E342"),sQuery(id+"F24.wireOp",EDGE,"E343"),sQuery(id+"F24.wireOp",EDGE,"E344"),sQuery(id+"F24.wireOp",EDGE,"E345.MirrorCS"),sQuery(id+"F24.wireOp",EDGE,"E346.MirrorCS"),sQuery(id+"F24.wireOp",EDGE,"E347.MirrorCS"),sQuery(id+"F24.wireOp",EDGE,"E348.MirrorCS"),sQuery(id+"F24.wireOp",EDGE,"E349.MirrorCS"),sQuery(id+"F24.wireOp",EDGE,"E350.MirrorCS"),sQuery(id+"F24.wireOp",EDGE,"E351.MirrorCS")])],"isStart":false});
            var sketch = newSketch(context, id + "F26", { "sketchPlane" : qUnion([Q0])});
            skCircle(sketch, "E352", {"center": v(0, 21.69) * mm, "radius": 7.94 * mm});
            skPoint(sketch, "E352.centerSnap0", {"position": v(0, 40.74) * mm});
            skCircle(sketch, "E353", {"center": v(16.15, 21.69) * mm, "radius": 1.59 * mm});
            skCircle(sketch, "E354", {"center": v(12.7, 34.39) * mm, "radius": 1.59 * mm});
            skCircle(sketch, "E355.MirrorC", {"center": v(-12.7, 34.39) * mm, "radius": 1.59 * mm});
            skCircle(sketch, "E356.MirrorC", {"center": v(-16.15, 21.69) * mm, "radius": 1.59 * mm});
            skSolve(sketch);
        }
        {
            var Q0;
            Q0 = qSketchRegion(id + "F26", true);
            var Q1;
            Q1=makeQuery(id+"F25.opExtrude","CAP_FACE",FACE,{"disambiguationData":[OSD([sQuery(id+"F24.wireOp",EDGE,"E338"),sQuery(id+"F24.wireOp",EDGE,"E339"),sQuery(id+"F24.wireOp",EDGE,"E340"),sQuery(id+"F24.wireOp",EDGE,"E341"),sQuery(id+"F24.wireOp",EDGE,"E342"),sQuery(id+"F24.wireOp",EDGE,"E343"),sQuery(id+"F24.wireOp",EDGE,"E344"),sQuery(id+"F24.wireOp",EDGE,"E345.MirrorCS"),sQuery(id+"F24.wireOp",EDGE,"E346.MirrorCS"),sQuery(id+"F24.wireOp",EDGE,"E347.MirrorCS"),sQuery(id+"F24.wireOp",EDGE,"E348.MirrorCS"),sQuery(id+"F24.wireOp",EDGE,"E349.MirrorCS"),sQuery(id+"F24.wireOp",EDGE,"E350.MirrorCS"),sQuery(id+"F24.wireOp",EDGE,"E351.MirrorCS")])],"isStart":true});
            extrude(context, id + "F27", {"entities" : qUnion([Q0]), "operationType" : NewBodyOperationType.REMOVE, "endBound" : BoundingType.UP_TO_SURFACE, "oppositeDirection" : true, "endBoundEntityFace" : qUnion([Q1]), "depth" : 25.4 * mm});
        }
        {
            var Q0;
            Q0=makeQuery(id+"F23.boolean.opBoolean","COPY",FACE,{"derivedFrom":makeQuery(id+"F23.opExtrude","SWEPT_FACE",FACE,{"disambiguationData":[OSD([sQuery(id+"F22.wireOp",EDGE,"E333")])]})});
            var sketch = newSketch(context, id + "F28", { "sketchPlane" : qUnion([Q0])});
            skLineSegment(sketch, "E357", {"start": v(0, 59.79) * mm, "end": v(6.35, 59.79) * mm});
            skLineSegment(sketch, "E358", {"start": v(6.35, 59.79) * mm, "end": v(6.35, 57.1) * mm});
            skLineSegment(sketch, "E359", {"start": v(6.35, 57.1) * mm, "end": v(19.81, 57.1) * mm});
            skLineSegment(sketch, "E360", {"start": v(19.81, 57.1) * mm, "end": v(19.81, 49.1) * mm});
            skLineSegment(sketch, "E361", {"start": v(19.81, 49.1) * mm, "end": v(22.35, 49.1) * mm});
            skLineSegment(sketch, "E362", {"start": v(22.35, 49.1) * mm, "end": v(22.35, 44.02) * mm});
            skLineSegment(sketch, "E363", {"start": v(22.35, 44.02) * mm, "end": v(0, 44.02) * mm});
            skLineSegment(sketch, "E364.MirrorCS", {"start": v(0, 59.79) * mm, "end": v(-6.35, 59.79) * mm});
            skLineSegment(sketch, "E365.MirrorCS", {"start": v(-6.35, 59.79) * mm, "end": v(-6.35, 57.1) * mm});
            skLineSegment(sketch, "E366.MirrorCS", {"start": v(-6.35, 57.1) * mm, "end": v(-19.81, 57.1) * mm});
            skLineSegment(sketch, "E367.MirrorCS", {"start": v(-19.81, 57.1) * mm, "end": v(-19.81, 49.1) * mm});
            skLineSegment(sketch, "E368.MirrorCS", {"start": v(-19.81, 49.1) * mm, "end": v(-22.35, 49.1) * mm});
            skLineSegment(sketch, "E369.MirrorCS", {"start": v(-22.35, 49.1) * mm, "end": v(-22.35, 44.02) * mm});
            skLineSegment(sketch, "E370.MirrorCS", {"start": v(-22.35, 44.02) * mm, "end": v(0, 44.02) * mm});
            skLineSegment(sketch, "E371", {"start": v(-12.7, 50.37) * mm, "end": v(12.7, 50.37) * mm, "construction": true});
            skPoint(sketch, "E372", {"position": v(0, 50.37) * mm});
            skSolve(sketch);
        }
        {
            var Q0;
            Q0 = qSketchRegion(id + "F28", true);
            extrude(context, id + "F29", {"entities" : qUnion([Q0]), "depth" : 2.7 * mm});
        }
        {
            var Q0;
            Q0=makeQuery(id+"F9.opExtrude","CAP_FACE",FACE,{"disambiguationData":[OSD([sQuery(id+"F8.wireOp",EDGE,"E88.0"),sQuery(id+"F8.wireOp",EDGE,"E88.1"),sQuery(id+"F8.wireOp",EDGE,"E88.2"),sQuery(id+"F8.wireOp",EDGE,"E88.3"),sQuery(id+"F8.wireOp",EDGE,"E89"),sQuery(id+"F8.wireOp",EDGE,"E90"),sQuery(id+"F8.wireOp",EDGE,"E91"),sQuery(id+"F8.wireOp",EDGE,"E92"),sQuery(id+"F8.wireOp",EDGE,"E94"),sQuery(id+"F8.wireOp",EDGE,"E95"),sQuery(id+"F8.wireOp",EDGE,"E96.filletArc"),sQuery(id+"F8.wireOp",EDGE,"E97.MirrorCS"),sQuery(id+"F8.wireOp",EDGE,"E98.MirrorCS"),sQuery(id+"F8.wireOp",EDGE,"E99.MirrorCS"),sQuery(id+"F8.wireOp",EDGE,"E100.MirrorCS"),sQuery(id+"F8.wireOp",EDGE,"E101.MirrorCS"),sQuery(id+"F8.wireOp",EDGE,"E102.MirrorCS"),sQuery(id+"F8.wireOp",EDGE,"E104.MirrorCS"),sQuery(id+"F8.wireOp",EDGE,"E105.MirrorCS"),sQuery(id+"F8.wireOp",EDGE,"E106.MirrorCS"),sQuery(id+"F8.wireOp",EDGE,"E107.MirrorCS"),sQuery(id+"F8.wireOp",EDGE,"E109.MirrorCS"),sQuery(id+"F8.wireOp",EDGE,"E110.MirrorCS"),sQuery(id+"F8.wireOp",EDGE,"E111.MirrorCS"),sQuery(id+"F8.wireOp",EDGE,"E112.MirrorCS"),sQuery(id+"F8.wireOp",EDGE,"E113.MirrorCS"),sQuery(id+"F8.wireOp",EDGE,"E114.MirrorCS"),sQuery(id+"F8.wireOp",EDGE,"E115.MirrorCS"),sQuery(id+"F8.wireOp",EDGE,"E116.MirrorCS"),sQuery(id+"F8.wireOp",EDGE,"E117.MirrorCS"),sQuery(id+"F8.wireOp",EDGE,"E118.MirrorCS"),sQuery(id+"F8.wireOp",EDGE,"E119.MirrorCS"),sQuery(id+"F8.wireOp",EDGE,"E120.MirrorCS"),sQuery(id+"F8.wireOp",EDGE,"E122.MirrorCS"),sQuery(id+"F8.wireOp",EDGE,"E124.MirrorCS"),sQuery(id+"F8.wireOp",EDGE,"E125.MirrorCS"),sQuery(id+"F8.wireOp",EDGE,"E126.MirrorCS"),sQuery(id+"F8.wireOp",EDGE,"E127.MirrorCS"),sQuery(id+"F8.wireOp",EDGE,"E128.MirrorCS"),sQuery(id+"F8.wireOp",EDGE,"E129.MirrorCS"),sQuery(id+"F8.wireOp",EDGE,"E130.MirrorCS"),sQuery(id+"F8.wireOp",EDGE,"E132.MirrorCS"),sQuery(id+"F8.wireOp",EDGE,"E134.MirrorCS"),sQuery(id+"F8.wireOp",EDGE,"E135.MirrorCS")])],"isStart":true});
            var sketch = newSketch(context, id + "F30", { "sketchPlane" : qUnion([Q0])});
            skLineSegment(sketch, "E373", {"start": v(10.39, -50.8) * mm, "end": v(1.59, -50.8) * mm});
            skLineSegment(sketch, "E374.0", {"start": v(-11.95, -52.66) * mm, "end": v(-11.62, -54.53) * mm});
            skArc(sketch, "E374.1", {"start": v(-8.5, -57.15) * mm, "mid": v(-10.54, -56.4) * mm, "end": v(-11.62, -54.53) * mm});
            skLineSegment(sketch, "E374.2", {"start": v(8.5, -57.15) * mm, "end": v(-8.5, -57.15) * mm});
            skArc(sketch, "E374.3", {"start": v(8.5, -57.15) * mm, "mid": v(10.54, -56.4) * mm, "end": v(11.62, -54.53) * mm});
            skLineSegment(sketch, "E374.4", {"start": v(11.95, -52.66) * mm, "end": v(11.62, -54.53) * mm});
            skArc(sketch, "E375.0", {"start": v(1.59, -50.8) * mm, "mid": v(0, -52.39) * mm, "end": v(-1.59, -50.8) * mm});
            skLineSegment(sketch, "E376.trimOffspring", {"start": v(-1.59, -50.8) * mm, "end": v(-10.39, -50.8) * mm});
            skPoint(sketch, "E377.visualSharp", {"position": v(12.28, -50.8) * mm});
            skArc(sketch, "E377.filletArc", {"start": v(11.95, -52.66) * mm, "mid": v(11.6, -51.37) * mm, "end": v(10.39, -50.8) * mm});
            skPoint(sketch, "E378.visualSharp", {"position": v(-12.28, -50.8) * mm});
            skArc(sketch, "E378.filletArc", {"start": v(-10.39, -50.8) * mm, "mid": v(-11.6, -51.37) * mm, "end": v(-11.95, -52.66) * mm});
            skSolve(sketch);
        }
        {
            var Q0;
            Q0 = qSketchRegion(id + "F30", true);
            extrude(context, id + "F31", {"entities" : qUnion([Q0]), "depth" : 2.7 * mm});
        }
        {
            var Q0;
            Q0=sQuery(id+"F28.wireOp",VERTEX,"E371.start");
            var Q1;
            Q1=sQuery(id+"F28.wireOp",VERTEX,"E371.end");
            var Q2;
            Q2=makeQuery(id+"F29.opExtrude","SWEPT_BODY",BODY,{"disambiguationData":[OSD([sQuery(id+"F28.wireOp",EDGE,"E357"),sQuery(id+"F28.wireOp",EDGE,"E358"),sQuery(id+"F28.wireOp",EDGE,"E359"),sQuery(id+"F28.wireOp",EDGE,"E360"),sQuery(id+"F28.wireOp",EDGE,"E361"),sQuery(id+"F28.wireOp",EDGE,"E362"),sQuery(id+"F28.wireOp",EDGE,"E363"),sQuery(id+"F28.wireOp",EDGE,"E364.MirrorCS"),sQuery(id+"F28.wireOp",EDGE,"E365.MirrorCS"),sQuery(id+"F28.wireOp",EDGE,"E366.MirrorCS"),sQuery(id+"F28.wireOp",EDGE,"E367.MirrorCS"),sQuery(id+"F28.wireOp",EDGE,"E368.MirrorCS"),sQuery(id+"F28.wireOp",EDGE,"E369.MirrorCS"),sQuery(id+"F28.wireOp",EDGE,"E370.MirrorCS")])]});
            hole(context, id + "F32", {"style" : HoleStyle.SIMPLE, "holeDiameter" : 3.17 * mm, "endStyle" : HoleEndStyle.THROUGH, "oppositeDirection" : true, "locations" : qUnion([Q0, Q1]), "scope" : qUnion([Q2])});
        }
    });
